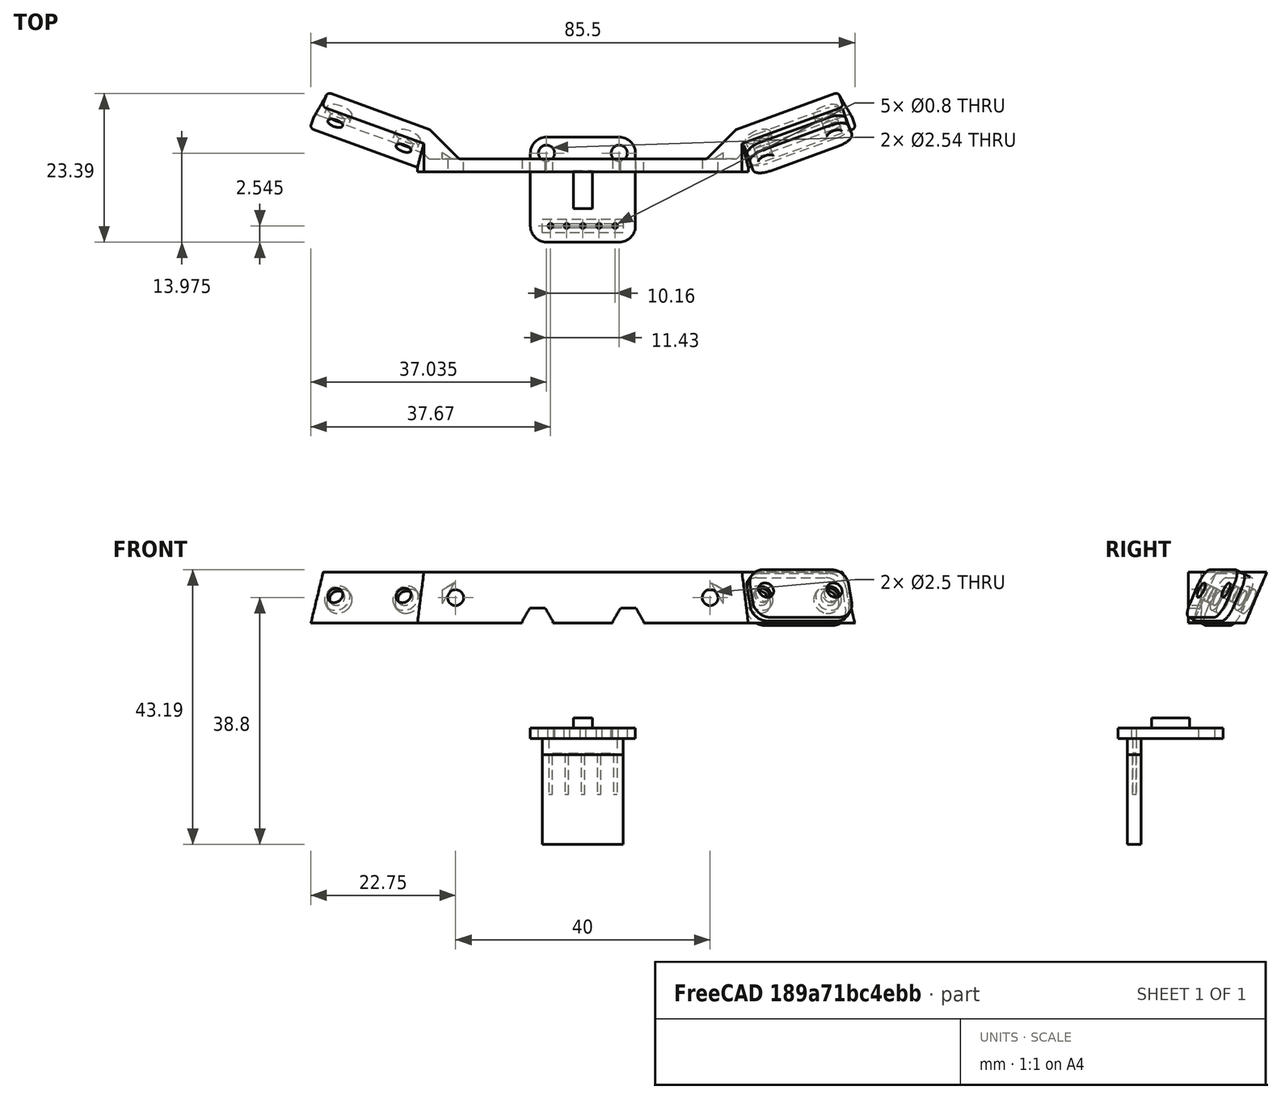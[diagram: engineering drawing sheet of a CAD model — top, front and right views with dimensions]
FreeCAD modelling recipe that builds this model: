
FCSTD DOCUMENT  (FreeCAD 0.19R24276 (Git))
Label: PB3D_Triplate_USMtToLightSens
License: All rights reserved
LicenseURL: http://en.wikipedia.org/wiki/All_rights_reserved
objects: Sketcher::SketchObject×29, PartDesign::Pocket×15, PartDesign::Body×13, PartDesign::Pad×12, PartDesign::Plane×11, PartDesign::LinearPattern×4, App::Part×3, Spreadsheet::Sheet×2, PartDesign::CoordinateSystem×2, Mesh::Feature×2, PartDesign::AdditiveLoft×1
note: 115 computed .brp shape members not serialized (recipe doc carries the construction recipe); baked Part::Feature solids carry a one-line shape summary decoded from their .brp

FEATURE [Spreadsheet::Sheet] Spreadsheet  label="params"
  cells = A1=M2 Bolt Clearances; C1=M2.5 Bolt Clearances; A2=Hole Clear Diam; B2(m2_hole_clear_diam)==2.5mm; C2=Hole Clear Diam; D2(m25_hole_clear_diam)==2.8mm; E2=Std Rad; F2(std_rad)==2mm; A3=Head Clear Diam; B3(m2_head_clear_diam)==4.2mm; C3=Head Clear Diam; D3(m25_head_clear_diam)==5.2mm; E3=Std Rad Min; F3(std_rad_min)==0.6mm; A4=Head Min Depth; B4(m2_head_min_depth)==2mm; C4=Head Min Depth; D4(m25_head_min_depth)==2.3mm; E4=Std Tol Clear; F4(std_tol_clear)==0.3mm; A5=Nut Clear Flat; B5(m2_nut_clear_flat)==4.2mm; C5=Nut Clear Flat; D5(m25_nut_clear_flat)==5.2mm; A6=Nut Min Depth; B6(m2_nut_min_depth)==2mm; C6=Nut Min Depth; D6(m25_nut_min_depth)==2mm; A8=USR Mount; C8=Light Sens Cent Loc; E8=LightMt; A9=USR Mt Width; B9(usr_mt_width)==52mm; C9=LightSens Loc X; D9(lightsens_loc_x)==35mm; E9=LightMt Side Thick; F9(lightmt_thick_side)==2.4mm; A10=USR Mt Height; B10(usr_mt_height)==41.5mm; C10=LightSens Loc Y; D10(lightsens_loc_y)==4.5mm; E10=LightMt Cent Thick; F10(lightmt_thick_cent)==2mm; A11=USR Mt Vert Thick; B11(usr_mt_vert_thick_top)==4.8mm; C11=LightSens Loc Z; D11(lightsens_loc_z)==16.5mm; E11=LightMt Leng Base; F11(lightmt_leng_base)==18mm; A12=USR Mt Vert Thick Bot; B12(usr_mt_vert_thick_bot)==8.4mm; C12=LightSens Ang X; D12(lightsens_ang_x)==65deg; E12=LightMt Leng Top; F12(lightmt_leng_top)==17mm; A13=USR Mt Foot Width; B13(usr_mt_foot_width)==32mm; C13=LightSens Ang Y; D13(lightsens_ang_y)==0deg; E13=LightMt Height; F13(lightmt_height)==8mm; C14=LightSens Ang Z; D14(lightsens_ang_z)==20deg; E14=LightMt Base Offset; F14(lightmt_base_offset)==3.5mm; A15=USR Mt Hole Cent Loc Z; B15(usr_mt_hole_cent_loc_z)==27mm; E15=LightMt Top Offset; F15(lightmt_top_offset)==lightmt_base_offset + lightmt_height / tan(lightsens_vert_slope_ang); A16=USR Mt Hole Width Long; B16(usr_mt_hole_width_long)==22.625mm; C16=LightSens Vert Slope Ang; D16(lightsens_vert_slope_ang)==lightsens_ang_x; E16=LightMt Z Dist to Mid Plate; F16(lightmt_z_dist_to_mid_plate)==3mm; A17=USR Mt Hole Width Short; B17(usr_mt_hole_width_short)==7.125mm; E17=LightMt Hole Space Leng; F17(lightmt_hole_space_leng)==40mm; A18=USR Mt Hole Height; B18(usr_mt_hole_height)==20.5mm; C18=LightSens Leng; D18(lightsens_leng)==16.51mm; C19=LightSens Width; D19(lightsens_width)==16.51mm; C20=LightSens Hole Width; D20(lightsens_hole_leng_space)==11.43mm; C21=LightSens Hole Edge Offset; D21(lightsens_hole_edge_offset)==2.54mm; C22=LightSens Hole Diam; D22(lightsens_hole_diam)==2.54mm
FEATURE [Spreadsheet::Sheet] Spreadsheet002  label="I2CLightParams"
  cells = A1=Inch to mm; B1(intomm)==25.4mm; E1=std tol; F1(std_tol)==0.3mm; A3=Adafruit I2C Exp; E3=Adafruit Temp I2C; I3=Adafruit Light; B4=Inch; C4=mm; F4=Inch; G4=mm; J4=Inch; K4=mm; A5=Length; B5=1.2; C5(exp_i2c_leng)==B5 * B$1; E5=Length; F5=0.8; G5(temp_leng)==F5 * $B$1; I5=Length; J5=0.65; K5(light_leng)==J5 * $B$1; A6=Width; B6=0.7; C6(exp_i2c_width)==B6 * B$1; E6=Width; F6=0.5; G6(temp_width)==F6 * $B$1; I6=Width; J6=0.65; K6(light_width)==J6 * $B$1; A7=Hole Leng Space; B7=1; C7(exp_i2c_hole_leng_space)==B7 * B$1; E7=Hole Leng Space; F7=0.6; G7(temp_hole_leng_space)==F7 * $B$1; I7=Hole Leng Space; J7=0.45; K7(light_hole_leng_space)==J7 * $B$1; A8=Hole Diam; B8=0.1; C8(exp_i2c_hole_mt_diam)==B8 * B$1; E8=Hole Diam; F8=0.1; G8(temp_hole_diam)==F8 * $B$1; I8=Hole Diam; J8=0.1; K8(light_hole_diam)==J8 * $B$1; A9=Num Pins; B9(exp_i2c_num_pins)=12; E9=Hole Edge Offset; F9=0.1; G9(temp_hole_edge_offset)==F9 * $B$1; I9=Hole Edge Offset; J9=0.1; K9(light_hole_edge_offset)==J9 * $B$1; A10=Pin Width Space; B10=0.6; C10(exp_i2c_pin_width_space)==B10 * B$1; E10=Pin Edge Offset; F10=0.09; G10(temp_pin_edge_offset)==F10 * $B$1; I10=Pin Edge Offset; J10=0.1; K10(light_pin_edge_offset)==J10 * $B$1; E11=Num Pins; F11(temp_num_pins)=8; I11=Num Pins; J11(light_num_pins)=5; A12=General Parameters; A13=Board Thick; B13(board_thickness)==1.65mm; A15=Pin Hole Diam; B15(pin_hole_diam)==0.8mm; A16=Pin Hole Space; B16(pin_hole_space)==2.54mm; A17=Pin Width; B17(pin_width)==0.6mm; A18=Pin Square Block Dim; B18(pin_square_block_dim)==2.54mm; A19=Pin Leng; B19(pin_leng)==6.2mm; A20=Pin Jumper Leng; B20(pin_jumper_leng)==14.1mm; A21=Pin Spacing; B21(pin_spacing)==2.54mm
FEATURE [Sketcher::SketchObject] Sketch049
  FullyConstrained = true
  MapMode = 5
  Support = -> [XY_Plane038]
  expr: Constraints[16] = <<I2CLightParams>>.light_leng
  expr: Constraints[17] = <<I2CLightParams>>.light_width
  expr: Constraints[18] = <<I2CLightParams>>.light_hole_diam
  sketch-geometry (8):
    g0: LineSegment StartX=-5.715 StartY=8.255 StartZ=0 EndX=5.715 EndY=8.255 EndZ=0
    g1: LineSegment StartX=8.255 StartY=5.715 StartZ=0 EndX=8.255 EndY=-5.715 EndZ=0
    g2: LineSegment StartX=5.715 StartY=-8.255 StartZ=0 EndX=-5.715 EndY=-8.255 EndZ=0
    g3: LineSegment StartX=-8.255 StartY=-5.715 StartZ=0 EndX=-8.255 EndY=5.715 EndZ=0
    g4: ArcOfCircle CenterX=-5.715 CenterY=5.715 CenterZ=0 NormalX=0 NormalY=0 NormalZ=1 AngleXU=0 Radius=2.54 StartAngle=1.5708 EndAngle=3.14159
    g5: ArcOfCircle CenterX=5.715 CenterY=5.715 CenterZ=0 NormalX=0 NormalY=0 NormalZ=1 AngleXU=0 Radius=2.54 StartAngle=1.76e-14 EndAngle=1.5708
    g6: ArcOfCircle CenterX=5.715 CenterY=-5.715 CenterZ=0 NormalX=0 NormalY=0 NormalZ=1 AngleXU=0 Radius=2.54 StartAngle=4.71239 EndAngle=6.28319
    g7: ArcOfCircle CenterX=-5.715 CenterY=-5.715 CenterZ=0 NormalX=0 NormalY=0 NormalZ=1 AngleXU=0 Radius=2.54 StartAngle=3.14159 EndAngle=4.71239
  constraints (19):
    c: Horizontal(g0)
    c: Horizontal(g2)
    c: Vertical(g1)
    c: Vertical(g3)
    c: Tangent(g3,g4) = 1.5708
    c: Tangent(g0,g4) = 1.5708
    c: Tangent(g0,g5) = 1.5708
    c: Tangent(g1,g5) = 1.5708
    c: Tangent(g1,g6) = 1.5708
    c: Tangent(g2,g6) = 1.5708
    c: Tangent(g2,g7) = 1.5708
    c: Tangent(g3,g7) = 1.5708
    c: Equal(g4,g5)
    c: Equal(g5,g6)
    c: Equal(g6,g7)
    c: Symmetric(g7,g5,g-1)
    c: DistanceX(g3,g1) = 16.51
    c: DistanceY(g2,g0) = 16.51
    c: Radius(g5) = 2.54
FEATURE [Sketcher::SketchObject] Sketch048
  FullyConstrained = true
  MapMode = 5
  Support = -> [XY_Plane037]
  sketch-geometry (4):
    g0: LineSegment StartX=-1.5 StartY=3 StartZ=0 EndX=1.5 EndY=3 EndZ=0
    g1: LineSegment StartX=1.5 StartY=3 StartZ=0 EndX=1.5 EndY=-3 EndZ=0
    g2: LineSegment StartX=1.5 StartY=-3 StartZ=0 EndX=-1.5 EndY=-3 EndZ=0
    g3: LineSegment StartX=-1.5 StartY=-3 StartZ=0 EndX=-1.5 EndY=3 EndZ=0
  constraints (11):
    c: Coincident(g0,g1)
    c: Coincident(g1,g2)
    c: Coincident(g2,g3)
    c: Coincident(g3,g0)
    c: Horizontal(g0)
    c: Horizontal(g2)
    c: Vertical(g1)
    c: Vertical(g3)
    c: Symmetric(g2,g0,g-1)
    c: DistanceX(g0,g0) = 3
    c: DistanceY(g1,g1) = 6
FEATURE [Sketcher::SketchObject] Sketch052
  FullyConstrained = true
  MapMode = 5
  Placement = pos=(0,0,0) rot=(1,0,0;1.5708rad)
  Support = -> [XZ_Plane034]
  expr: Constraints[57] = <<I2CLightParams>>.pin_leng * 2
  expr: Constraints[58] = <<I2CLightParams>>.pin_square_block_dim - <<I2CLightParams>>.std_tol
  expr: Constraints[59] = <<I2CLightParams>>.pin_width
  expr: Constraints[61] = <<I2CLightParams>>.pin_spacing
  sketch-geometry (24):
    g0: LineSegment StartX=-2.24 StartY=14.64 StartZ=0 EndX=-0.3 EndY=14.64 EndZ=0
    g1: LineSegment StartX=-0.3 StartY=14.64 StartZ=0 EndX=-0.3 EndY=2.24 EndZ=0
    g2: LineSegment StartX=-0.3 StartY=2.24 StartZ=0 EndX=-2.24 EndY=2.24 EndZ=0
    g3: LineSegment StartX=-2.24 StartY=2.24 StartZ=0 EndX=-2.24 EndY=14.64 EndZ=0
    g4: LineSegment StartX=0.3 StartY=14.64 StartZ=0 EndX=2.24 EndY=14.64 EndZ=0
    g5: LineSegment StartX=2.24 StartY=14.64 StartZ=0 EndX=2.24 EndY=2.24 EndZ=0
    g6: LineSegment StartX=2.24 StartY=2.24 StartZ=0 EndX=0.3 EndY=2.24 EndZ=0
    g7: LineSegment StartX=0.3 StartY=2.24 StartZ=0 EndX=0.3 EndY=14.64 EndZ=0
    g8: LineSegment StartX=2.84 StartY=14.64 StartZ=0 EndX=4.78 EndY=14.64 EndZ=0
    g9: LineSegment StartX=4.78 StartY=14.64 StartZ=0 EndX=4.78 EndY=2.24 EndZ=0
    g10: LineSegment StartX=4.78 StartY=2.24 StartZ=0 EndX=2.84 EndY=2.24 EndZ=0
    g11: LineSegment StartX=2.84 StartY=2.24 StartZ=0 EndX=2.84 EndY=14.64 EndZ=0
    g12: LineSegment StartX=-4.78 StartY=14.64 StartZ=0 EndX=-2.84 EndY=14.64 EndZ=0
    g13: LineSegment StartX=-2.84 StartY=14.64 StartZ=0 EndX=-2.84 EndY=2.24 EndZ=0
    g14: LineSegment StartX=-2.84 StartY=2.24 StartZ=0 EndX=-4.78 EndY=2.24 EndZ=0
    g15: LineSegment StartX=-4.78 StartY=2.24 StartZ=0 EndX=-4.78 EndY=14.64 EndZ=0
    g16: LineSegment StartX=-2.84 StartY=14.64 StartZ=0 EndX=-2.24 EndY=14.64 EndZ=0
    g17: LineSegment StartX=-0.3 StartY=14.64 StartZ=0 EndX=0.3 EndY=14.64 EndZ=0
    g18: LineSegment StartX=2.24 StartY=14.64 StartZ=0 EndX=2.84 EndY=14.64 EndZ=0
    g19: LineSegment StartX=-2.84 StartY=2.24 StartZ=0 EndX=-2.24 EndY=2.24 EndZ=0
    g20: LineSegment StartX=-0.3 StartY=2.24 StartZ=0 EndX=0.3 EndY=2.24 EndZ=0
    g21: LineSegment StartX=2.24 StartY=2.24 StartZ=0 EndX=2.84 EndY=2.24 EndZ=0
    g22: GeomPoint X=0 Y=2.24 Z=0
    g23: GeomPoint X=2.54 Y=2.24 Z=0
  constraints (62):
    c: Coincident(g0,g1)
    c: Coincident(g1,g2)
    c: Coincident(g2,g3)
    c: Coincident(g3,g0)
    c: Horizontal(g0)
    c: Horizontal(g2)
    c: Vertical(g1)
    c: Vertical(g3)
    c: Coincident(g4,g5)
    c: Coincident(g5,g6)
    c: Coincident(g6,g7)
    c: Coincident(g7,g4)
    c: Horizontal(g4)
    c: Horizontal(g6)
    c: Vertical(g5)
    c: Vertical(g7)
    c: Coincident(g8,g9)
    c: Coincident(g9,g10)
    c: Coincident(g10,g11)
    c: Coincident(g11,g8)
    c: Horizontal(g8)
    c: Horizontal(g10)
    c: Vertical(g9)
    c: Vertical(g11)
    c: Coincident(g12,g13)
    c: Coincident(g13,g14)
    c: Coincident(g14,g15)
    c: Coincident(g15,g12)
    c: Horizontal(g12)
    c: Horizontal(g14)
    c: Vertical(g13)
    c: Vertical(g15)
    c: Equal(g12,g0)
    c: Equal(g0,g4)
    c: Equal(g4,g8)
    c: Coincident(g16,g12)
    c: Coincident(g16,g0)
    c: Coincident(g17,g0)
    c: Coincident(g17,g4)
    c: Horizontal(g17)
    c: Coincident(g18,g4)
    c: Coincident(g18,g8)
    c: Horizontal(g18)
    c: Coincident(g19,g13)
    c: Coincident(g19,g2)
    c: Coincident(g20,g1)
    c: Coincident(g20,g6)
    c: Coincident(g21,g5)
    c: Coincident(g21,g10)
    c: Equal(g16,g17)
    c: Equal(g17,g18)
    c: Horizontal(g16)
    c: Horizontal(g19)
    c: Horizontal(g20)
    c: Horizontal(g21)
    c: PointOnObject(g22,g-2)
    c: Symmetric(g1,g6,g22)
    c: DistanceY(g9,g9) = 12.4
    c: DistanceY(g-1,g22) = 2.24
    c: DistanceX(g17,g17) = 0.6
    c: Symmetric(g5,g10,g23)
    c: DistanceX(g22,g23) = 2.54
FEATURE [Sketcher::SketchObject] Sketch050
  FullyConstrained = true
  MapMode = 5
  Support = -> [XY_Plane038]
  expr: Constraints[6] = <<I2CLightParams>>.light_hole_diam
  expr: Constraints[7] = <<I2CLightParams>>.light_hole_leng_space
  expr: Constraints[8] = <<I2CLightParams>>.light_width / 2 - <<I2CLightParams>>.light_hole_edge_offset
  sketch-geometry (4):
    g0: Circle CenterX=-5.715 CenterY=5.715 CenterZ=0 NormalX=0 NormalY=0 NormalZ=1 AngleXU=0 Radius=1.27
    g1: Circle CenterX=5.715 CenterY=5.715 CenterZ=0 NormalX=0 NormalY=0 NormalZ=1 AngleXU=0 Radius=1.27
    g2: LineSegment StartX=-5.715 StartY=5.715 StartZ=0 EndX=5.715 EndY=5.715 EndZ=0
    g3: GeomPoint X=0 Y=5.715 Z=0
  constraints (9):
    c: Coincident(g2,g0)
    c: Coincident(g2,g1)
    c: Horizontal(g2)
    c: PointOnObject(g3,g-2)
    c: Symmetric(g0,g1,g3)
    c: Equal(g0,g1)
    c: Diameter(g1) = 2.54
    c: DistanceX(g2,g2) = 11.43
    c: DistanceY(g-1,g3) = 5.715
FEATURE [Sketcher::SketchObject] Sketch051
  FullyConstrained = true
  MapMode = 5
  Support = -> [XY_Plane038]
  expr: Constraints[2] = <<I2CLightParams>>.pin_hole_diam
  expr: Constraints[1] = <<I2CLightParams>>.light_width / 2 - <<I2CLightParams>>.light_hole_edge_offset
  sketch-geometry (1):
    g0: Circle CenterX=0 CenterY=-5.715 CenterZ=0 NormalX=0 NormalY=0 NormalZ=1 AngleXU=0 Radius=0.4
  constraints (3):
    c: PointOnObject(g0,g-2)
    c: DistanceY(g0,g-1) = 5.715
    c: Diameter(g0) = 0.8
FEATURE [Sketcher::SketchObject] Sketch057
  FullyConstrained = true
  MapMode = 5
  Support = -> [XY_Plane044]
  expr: Constraints[1] = <<I2CLightParams>>.light_width / 2 - <<I2CLightParams>>.light_hole_edge_offset
  expr: Constraints[2] = <<I2CLightParams>>.pin_hole_diam
  sketch-geometry (1):
    g0: Circle CenterX=0 CenterY=-5.715 CenterZ=0 NormalX=0 NormalY=0 NormalZ=1 AngleXU=0 Radius=0.4
  constraints (3):
    c: PointOnObject(g0,g-2)
    c: DistanceY(g0,g-1) = 5.715
    c: Diameter(g0) = 0.8
FEATURE [Sketcher::SketchObject] Sketch055
  FullyConstrained = true
  MapMode = 5
  Support = -> [XY_Plane033]
  expr: Constraints[12] = <<I2CLightParams>>.pin_square_block_dim * (<<I2CLightParams>>.light_num_pins - 1) + <<I2CLightParams>>.pin_width
  expr: Constraints[11] = <<I2CLightParams>>.pin_width
  expr: Constraints[10] = <<I2CLightParams>>.light_width / 2 - <<I2CLightParams>>.light_hole_edge_offset
  sketch-geometry (5):
    g0: LineSegment StartX=-5.38 StartY=-5.415 StartZ=0 EndX=5.38 EndY=-5.415 EndZ=0
    g1: LineSegment StartX=5.38 StartY=-5.415 StartZ=0 EndX=5.38 EndY=-6.015 EndZ=0
    g2: LineSegment StartX=5.38 StartY=-6.015 StartZ=0 EndX=-5.38 EndY=-6.015 EndZ=0
    g3: LineSegment StartX=-5.38 StartY=-6.015 StartZ=0 EndX=-5.38 EndY=-5.415 EndZ=0
    g4: GeomPoint X=0 Y=-5.715 Z=0
  constraints (13):
    c: Coincident(g0,g1)
    c: Coincident(g1,g2)
    c: Coincident(g2,g3)
    c: Coincident(g3,g0)
    c: Horizontal(g0)
    c: Horizontal(g2)
    c: Vertical(g1)
    c: Vertical(g3)
    c: PointOnObject(g4,g-2)
    c: Symmetric(g2,g0,g4)
    c: DistanceY(g4,g-1) = 5.715
    c: DistanceY(g1,g1) = 0.6
    c: DistanceX(g2,g2) = 10.76
FEATURE [Sketcher::SketchObject] Sketch053
  FullyConstrained = false
  MapMode = 5
  Support = -> [XY_Plane035]
  expr: Constraints[11] = <<I2CLightParams>>.light_width / 2 - <<I2CLightParams>>.light_hole_edge_offset
  expr: Constraints[10] = <<I2CLightParams>>.pin_square_block_dim * <<I2CLightParams>>.light_num_pins
  sketch-geometry (5):
    g0: LineSegment StartX=-6.35 StartY=-4.6212 StartZ=0 EndX=6.35 EndY=-4.6212 EndZ=0
    g1: LineSegment StartX=6.35 StartY=-4.6212 StartZ=0 EndX=6.35 EndY=-6.8088 EndZ=0
    g2: LineSegment StartX=6.35 StartY=-6.8088 StartZ=0 EndX=-6.35 EndY=-6.8088 EndZ=0
    g3: LineSegment StartX=-6.35 StartY=-6.8088 StartZ=0 EndX=-6.35 EndY=-4.6212 EndZ=0
    g4: GeomPoint X=0 Y=-5.715 Z=0
  constraints (12):
    c: Coincident(g0,g1)
    c: Coincident(g1,g2)
    c: Coincident(g2,g3)
    c: Coincident(g3,g0)
    c: Horizontal(g0)
    c: Horizontal(g2)
    c: Vertical(g1)
    c: Vertical(g3)
    c: PointOnObject(g4,g-2)
    c: Symmetric(g2,g0,g4)
    c: DistanceX(g2,g2) = 12.7
    c: DistanceY(g4,g-1) = 5.715
FEATURE [Sketcher::SketchObject] Sketch054
  FullyConstrained = false
  MapMode = 5
  Support = -> [XY_Plane034]
  expr: Constraints[10] = <<I2CLightParams>>.pin_square_block_dim * <<I2CLightParams>>.light_num_pins
  expr: Constraints[11] = <<I2CLightParams>>.light_width / 2 - <<I2CLightParams>>.light_hole_edge_offset
  sketch-geometry (5):
    g0: LineSegment StartX=-6.35 StartY=-4.6212 StartZ=0 EndX=6.35 EndY=-4.6212 EndZ=0
    g1: LineSegment StartX=6.35 StartY=-4.6212 StartZ=0 EndX=6.35 EndY=-6.8088 EndZ=0
    g2: LineSegment StartX=6.35 StartY=-6.8088 StartZ=0 EndX=-6.35 EndY=-6.8088 EndZ=0
    g3: LineSegment StartX=-6.35 StartY=-6.8088 StartZ=0 EndX=-6.35 EndY=-4.6212 EndZ=0
    g4: GeomPoint X=0 Y=-5.715 Z=0
  constraints (12):
    c: Coincident(g0,g1)
    c: Coincident(g1,g2)
    c: Coincident(g2,g3)
    c: Coincident(g3,g0)
    c: Horizontal(g0)
    c: Horizontal(g2)
    c: Vertical(g1)
    c: Vertical(g3)
    c: PointOnObject(g4,g-2)
    c: Symmetric(g2,g0,g4)
    c: DistanceX(g2,g2) = 12.7
    c: DistanceY(g4,g-1) = 5.715
FEATURE [Sketcher::SketchObject] Sketch056
  FullyConstrained = true
  MapMode = 5
  Support = -> [XY_Plane039]
  sketch-geometry (4):
    g0: LineSegment StartX=-1.5 StartY=3 StartZ=0 EndX=1.5 EndY=3 EndZ=0
    g1: LineSegment StartX=1.5 StartY=3 StartZ=0 EndX=1.5 EndY=-3 EndZ=0
    g2: LineSegment StartX=1.5 StartY=-3 StartZ=0 EndX=-1.5 EndY=-3 EndZ=0
    g3: LineSegment StartX=-1.5 StartY=-3 StartZ=0 EndX=-1.5 EndY=3 EndZ=0
  constraints (11):
    c: Coincident(g0,g1)
    c: Coincident(g1,g2)
    c: Coincident(g2,g3)
    c: Coincident(g3,g0)
    c: Horizontal(g0)
    c: Horizontal(g2)
    c: Vertical(g1)
    c: Vertical(g3)
    c: Symmetric(g2,g0,g-1)
    c: DistanceX(g0,g0) = 3
    c: DistanceY(g1,g1) = 6
FEATURE [Sketcher::SketchObject] Sketch058
  FullyConstrained = true
  MapMode = 5
  Placement = pos=(0,0,0) rot=(1,0,0;1.5708rad)
  Support = -> [XZ_Plane042]
  expr: Constraints[61] = <<I2CLightParams>>.pin_spacing
  expr: Constraints[59] = <<I2CLightParams>>.pin_width
  expr: Constraints[58] = <<I2CLightParams>>.pin_square_block_dim - <<I2CLightParams>>.std_tol
  expr: Constraints[57] = <<I2CLightParams>>.pin_leng * 2
  sketch-geometry (24):
    g0: LineSegment StartX=-2.24 StartY=14.64 StartZ=0 EndX=-0.3 EndY=14.64 EndZ=0
    g1: LineSegment StartX=-0.3 StartY=14.64 StartZ=0 EndX=-0.3 EndY=2.24 EndZ=0
    g2: LineSegment StartX=-0.3 StartY=2.24 StartZ=0 EndX=-2.24 EndY=2.24 EndZ=0
    g3: LineSegment StartX=-2.24 StartY=2.24 StartZ=0 EndX=-2.24 EndY=14.64 EndZ=0
    g4: LineSegment StartX=0.3 StartY=14.64 StartZ=0 EndX=2.24 EndY=14.64 EndZ=0
    g5: LineSegment StartX=2.24 StartY=14.64 StartZ=0 EndX=2.24 EndY=2.24 EndZ=0
    g6: LineSegment StartX=2.24 StartY=2.24 StartZ=0 EndX=0.3 EndY=2.24 EndZ=0
    g7: LineSegment StartX=0.3 StartY=2.24 StartZ=0 EndX=0.3 EndY=14.64 EndZ=0
    g8: LineSegment StartX=2.84 StartY=14.64 StartZ=0 EndX=4.78 EndY=14.64 EndZ=0
    g9: LineSegment StartX=4.78 StartY=14.64 StartZ=0 EndX=4.78 EndY=2.24 EndZ=0
    g10: LineSegment StartX=4.78 StartY=2.24 StartZ=0 EndX=2.84 EndY=2.24 EndZ=0
    g11: LineSegment StartX=2.84 StartY=2.24 StartZ=0 EndX=2.84 EndY=14.64 EndZ=0
    g12: LineSegment StartX=-4.78 StartY=14.64 StartZ=0 EndX=-2.84 EndY=14.64 EndZ=0
    g13: LineSegment StartX=-2.84 StartY=14.64 StartZ=0 EndX=-2.84 EndY=2.24 EndZ=0
    g14: LineSegment StartX=-2.84 StartY=2.24 StartZ=0 EndX=-4.78 EndY=2.24 EndZ=0
    g15: LineSegment StartX=-4.78 StartY=2.24 StartZ=0 EndX=-4.78 EndY=14.64 EndZ=0
    g16: LineSegment StartX=-2.84 StartY=14.64 StartZ=0 EndX=-2.24 EndY=14.64 EndZ=0
    g17: LineSegment StartX=-0.3 StartY=14.64 StartZ=0 EndX=0.3 EndY=14.64 EndZ=0
    g18: LineSegment StartX=2.24 StartY=14.64 StartZ=0 EndX=2.84 EndY=14.64 EndZ=0
    g19: LineSegment StartX=-2.84 StartY=2.24 StartZ=0 EndX=-2.24 EndY=2.24 EndZ=0
    g20: LineSegment StartX=-0.3 StartY=2.24 StartZ=0 EndX=0.3 EndY=2.24 EndZ=0
    g21: LineSegment StartX=2.24 StartY=2.24 StartZ=0 EndX=2.84 EndY=2.24 EndZ=0
    g22: GeomPoint X=0 Y=2.24 Z=0
    g23: GeomPoint X=2.54 Y=2.24 Z=0
  constraints (62):
    c: Coincident(g0,g1)
    c: Coincident(g1,g2)
    c: Coincident(g2,g3)
    c: Coincident(g3,g0)
    c: Horizontal(g0)
    c: Horizontal(g2)
    c: Vertical(g1)
    c: Vertical(g3)
    c: Coincident(g4,g5)
    c: Coincident(g5,g6)
    c: Coincident(g6,g7)
    c: Coincident(g7,g4)
    c: Horizontal(g4)
    c: Horizontal(g6)
    c: Vertical(g5)
    c: Vertical(g7)
    c: Coincident(g8,g9)
    c: Coincident(g9,g10)
    c: Coincident(g10,g11)
    c: Coincident(g11,g8)
    c: Horizontal(g8)
    c: Horizontal(g10)
    c: Vertical(g9)
    c: Vertical(g11)
    c: Coincident(g12,g13)
    c: Coincident(g13,g14)
    c: Coincident(g14,g15)
    c: Coincident(g15,g12)
    c: Horizontal(g12)
    c: Horizontal(g14)
    c: Vertical(g13)
    c: Vertical(g15)
    c: Equal(g12,g0)
    c: Equal(g0,g4)
    c: Equal(g4,g8)
    c: Coincident(g16,g12)
    c: Coincident(g16,g0)
    c: Coincident(g17,g0)
    c: Coincident(g17,g4)
    c: Horizontal(g17)
    c: Coincident(g18,g4)
    c: Coincident(g18,g8)
    c: Horizontal(g18)
    c: Coincident(g19,g13)
    c: Coincident(g19,g2)
    c: Coincident(g20,g1)
    c: Coincident(g20,g6)
    c: Coincident(g21,g5)
    c: Coincident(g21,g10)
    c: Equal(g16,g17)
    c: Equal(g17,g18)
    c: Horizontal(g16)
    c: Horizontal(g19)
    c: Horizontal(g20)
    c: Horizontal(g21)
    c: PointOnObject(g22,g-2)
    c: Symmetric(g1,g6,g22)
    c: DistanceY(g9,g9) = 12.4
    c: DistanceY(g-1,g22) = 2.24
    c: DistanceX(g17,g17) = 0.6
    c: Symmetric(g5,g10,g23)
    c: DistanceX(g22,g23) = 2.54
FEATURE [Sketcher::SketchObject] Sketch061
  FullyConstrained = false
  MapMode = 5
  Support = -> [XY_Plane042]
  expr: Constraints[11] = <<I2CLightParams>>.light_width / 2 - <<I2CLightParams>>.light_hole_edge_offset
  expr: Constraints[10] = <<I2CLightParams>>.pin_square_block_dim * <<I2CLightParams>>.light_num_pins
  sketch-geometry (5):
    g0: LineSegment StartX=-6.35 StartY=-4.6212 StartZ=0 EndX=6.35 EndY=-4.6212 EndZ=0
    g1: LineSegment StartX=6.35 StartY=-4.6212 StartZ=0 EndX=6.35 EndY=-6.8088 EndZ=0
    g2: LineSegment StartX=6.35 StartY=-6.8088 StartZ=0 EndX=-6.35 EndY=-6.8088 EndZ=0
    g3: LineSegment StartX=-6.35 StartY=-6.8088 StartZ=0 EndX=-6.35 EndY=-4.6212 EndZ=0
    g4: GeomPoint X=0 Y=-5.715 Z=0
  constraints (12):
    c: Coincident(g0,g1)
    c: Coincident(g1,g2)
    c: Coincident(g2,g3)
    c: Coincident(g3,g0)
    c: Horizontal(g0)
    c: Horizontal(g2)
    c: Vertical(g1)
    c: Vertical(g3)
    c: PointOnObject(g4,g-2)
    c: Symmetric(g2,g0,g4)
    c: DistanceX(g2,g2) = 12.7
    c: DistanceY(g4,g-1) = 5.715
FEATURE [Sketcher::SketchObject] Sketch059
  FullyConstrained = true
  MapMode = 5
  Support = -> [XY_Plane044]
  expr: Constraints[8] = <<I2CLightParams>>.light_width / 2 - <<I2CLightParams>>.light_hole_edge_offset
  expr: Constraints[7] = <<I2CLightParams>>.light_hole_leng_space
  expr: Constraints[6] = <<I2CLightParams>>.light_hole_diam
  sketch-geometry (4):
    g0: Circle CenterX=-5.715 CenterY=5.715 CenterZ=0 NormalX=0 NormalY=0 NormalZ=1 AngleXU=0 Radius=1.27
    g1: Circle CenterX=5.715 CenterY=5.715 CenterZ=0 NormalX=0 NormalY=0 NormalZ=1 AngleXU=0 Radius=1.27
    g2: LineSegment StartX=-5.715 StartY=5.715 StartZ=0 EndX=5.715 EndY=5.715 EndZ=0
    g3: GeomPoint X=0 Y=5.715 Z=0
  constraints (9):
    c: Coincident(g2,g0)
    c: Coincident(g2,g1)
    c: Horizontal(g2)
    c: PointOnObject(g3,g-2)
    c: Symmetric(g0,g1,g3)
    c: Equal(g0,g1)
    c: Diameter(g1) = 2.54
    c: DistanceX(g2,g2) = 11.43
    c: DistanceY(g-1,g3) = 5.715
FEATURE [Sketcher::SketchObject] Sketch060
  FullyConstrained = true
  MapMode = 5
  Support = -> [XY_Plane044]
  expr: Constraints[18] = <<I2CLightParams>>.light_hole_diam
  expr: Constraints[17] = <<I2CLightParams>>.light_width
  expr: Constraints[16] = <<I2CLightParams>>.light_leng
  sketch-geometry (8):
    g0: LineSegment StartX=-5.715 StartY=8.255 StartZ=0 EndX=5.715 EndY=8.255 EndZ=0
    g1: LineSegment StartX=8.255 StartY=5.715 StartZ=0 EndX=8.255 EndY=-5.715 EndZ=0
    g2: LineSegment StartX=5.715 StartY=-8.255 StartZ=0 EndX=-5.715 EndY=-8.255 EndZ=0
    g3: LineSegment StartX=-8.255 StartY=-5.715 StartZ=0 EndX=-8.255 EndY=5.715 EndZ=0
    g4: ArcOfCircle CenterX=-5.715 CenterY=5.715 CenterZ=0 NormalX=0 NormalY=0 NormalZ=1 AngleXU=0 Radius=2.54 StartAngle=1.5708 EndAngle=3.14159
    g5: ArcOfCircle CenterX=5.715 CenterY=5.715 CenterZ=0 NormalX=0 NormalY=0 NormalZ=1 AngleXU=0 Radius=2.54 StartAngle=1.76e-14 EndAngle=1.5708
    g6: ArcOfCircle CenterX=5.715 CenterY=-5.715 CenterZ=0 NormalX=0 NormalY=0 NormalZ=1 AngleXU=0 Radius=2.54 StartAngle=4.71239 EndAngle=6.28319
    g7: ArcOfCircle CenterX=-5.715 CenterY=-5.715 CenterZ=0 NormalX=0 NormalY=0 NormalZ=1 AngleXU=0 Radius=2.54 StartAngle=3.14159 EndAngle=4.71239
  constraints (19):
    c: Horizontal(g0)
    c: Horizontal(g2)
    c: Vertical(g1)
    c: Vertical(g3)
    c: Tangent(g3,g4) = 1.5708
    c: Tangent(g0,g4) = 1.5708
    c: Tangent(g0,g5) = 1.5708
    c: Tangent(g1,g5) = 1.5708
    c: Tangent(g1,g6) = 1.5708
    c: Tangent(g2,g6) = 1.5708
    c: Tangent(g2,g7) = 1.5708
    c: Tangent(g3,g7) = 1.5708
    c: Equal(g4,g5)
    c: Equal(g5,g6)
    c: Equal(g6,g7)
    c: Symmetric(g7,g5,g-1)
    c: DistanceX(g3,g1) = 16.51
    c: DistanceY(g2,g0) = 16.51
    c: Radius(g5) = 2.54
FEATURE [Sketcher::SketchObject] Sketch063
  FullyConstrained = false
  MapMode = 5
  Support = -> [XY_Plane041]
  expr: Constraints[10] = <<I2CLightParams>>.pin_square_block_dim * <<I2CLightParams>>.light_num_pins
  expr: Constraints[11] = <<I2CLightParams>>.light_width / 2 - <<I2CLightParams>>.light_hole_edge_offset
  sketch-geometry (5):
    g0: LineSegment StartX=-6.35 StartY=-4.6212 StartZ=0 EndX=6.35 EndY=-4.6212 EndZ=0
    g1: LineSegment StartX=6.35 StartY=-4.6212 StartZ=0 EndX=6.35 EndY=-6.8088 EndZ=0
    g2: LineSegment StartX=6.35 StartY=-6.8088 StartZ=0 EndX=-6.35 EndY=-6.8088 EndZ=0
    g3: LineSegment StartX=-6.35 StartY=-6.8088 StartZ=0 EndX=-6.35 EndY=-4.6212 EndZ=0
    g4: GeomPoint X=0 Y=-5.715 Z=0
  constraints (12):
    c: Coincident(g0,g1)
    c: Coincident(g1,g2)
    c: Coincident(g2,g3)
    c: Coincident(g3,g0)
    c: Horizontal(g0)
    c: Horizontal(g2)
    c: Vertical(g1)
    c: Vertical(g3)
    c: PointOnObject(g4,g-2)
    c: Symmetric(g2,g0,g4)
    c: DistanceX(g2,g2) = 12.7
    c: DistanceY(g4,g-1) = 5.715
FEATURE [Sketcher::SketchObject] Sketch062
  FullyConstrained = true
  MapMode = 5
  Support = -> [XY_Plane043]
  expr: Constraints[10] = <<I2CLightParams>>.light_width / 2 - <<I2CLightParams>>.light_hole_edge_offset
  expr: Constraints[11] = <<I2CLightParams>>.pin_width
  expr: Constraints[12] = <<I2CLightParams>>.pin_square_block_dim * (<<I2CLightParams>>.light_num_pins - 1) + <<I2CLightParams>>.pin_width
  sketch-geometry (5):
    g0: LineSegment StartX=-5.38 StartY=-5.415 StartZ=0 EndX=5.38 EndY=-5.415 EndZ=0
    g1: LineSegment StartX=5.38 StartY=-5.415 StartZ=0 EndX=5.38 EndY=-6.015 EndZ=0
    g2: LineSegment StartX=5.38 StartY=-6.015 StartZ=0 EndX=-5.38 EndY=-6.015 EndZ=0
    g3: LineSegment StartX=-5.38 StartY=-6.015 StartZ=0 EndX=-5.38 EndY=-5.415 EndZ=0
    g4: GeomPoint X=0 Y=-5.715 Z=0
  constraints (13):
    c: Coincident(g0,g1)
    c: Coincident(g1,g2)
    c: Coincident(g2,g3)
    c: Coincident(g3,g0)
    c: Horizontal(g0)
    c: Horizontal(g2)
    c: Vertical(g1)
    c: Vertical(g3)
    c: PointOnObject(g4,g-2)
    c: Symmetric(g2,g0,g4)
    c: DistanceY(g4,g-1) = 5.715
    c: DistanceY(g1,g1) = 0.6
    c: DistanceX(g2,g2) = 10.76
FEATURE [PartDesign::Pad] Pad027
  Direction = (1,1,1)
  Length = 1.6
  Length2 = 100
  Profile = -> Sketch056
  Type = 0
FEATURE [PartDesign::Body] Body034  label="LightSensor001"
  Group = -> [Sketch056,Pad027]
  Origin = -> Origin039
  Tip = -> Pad027
FEATURE [PartDesign::Pad] Pad020
  Direction = (1,1,1)
  Length = 1.6
  Length2 = 100
  Profile = -> Sketch048
  Type = 0
FEATURE [PartDesign::Body] Body031  label="LightSensor"
  Group = -> [Sketch048,Pad020]
  Origin = -> Origin034
  Tip = -> Pad020
FEATURE [PartDesign::Pad] Pad021
  Direction = (1,1,1)
  Length = 14.1
  Length2 = 100
  Profile = -> Sketch053
  Reversed = true
  Type = 0
  expr: Length = <<I2CLightParams>>.pin_jumper_leng
FEATURE [PartDesign::Body] Body032  label="JumperHeader002"
  Group = -> [Sketch053,Pad021]
  Origin = -> Origin038
  Placement = pos=(0,0,-4.2) rot=(0,0,1;0rad)
  Tip = -> Pad021
FEATURE [PartDesign::Pad] Pad022
  Direction = (1,1,1)
  Length = 2.54
  Length2 = 100
  Profile = -> Sketch054
  Type = 0
  expr: Length = <<I2CLightParams>>.pin_square_block_dim
FEATURE [PartDesign::Body] Body028  label="PinBlock002"
  Group = -> [Sketch054,Pad022]
  Origin = -> Origin037
  Placement = pos=(0,0,-4.2) rot=(0,0,1;0rad)
  Tip = -> Pad022
FEATURE [PartDesign::Pad] Pad024
  Direction = (1,1,1)
  Length = 8.74
  Length2 = 100
  Profile = -> Sketch062
  Type = 0
  expr: Length = <<I2CLightParams>>.pin_square_block_dim + <<I2CLightParams>>.pin_leng
FEATURE [PartDesign::Pocket] Pocket031
  BaseFeature = -> Pad024
  Length = 5
  Length2 = 100
  Midplane = true
  Profile = -> Sketch058
  Type = 1
FEATURE [PartDesign::Body] Body036  label="Pins003"
  Group = -> [Sketch062,Pad024,Sketch058,Pocket031]
  Origin = -> Origin041
  Placement = pos=(0,-11.4,-1.7) rot=(1,0,0;3.14159rad)
  Tip = -> Pocket031
FEATURE [PartDesign::Pad] Pad025
  Direction = (1,1,1)
  Length = 2.54
  Length2 = 100
  Profile = -> Sketch061
  Type = 0
  expr: Length = <<I2CLightParams>>.pin_square_block_dim
FEATURE [PartDesign::Body] Body035  label="PinBlock003"
  Group = -> [Sketch061,Pad025]
  Origin = -> Origin042
  Placement = pos=(0,0,-4.2) rot=(0,0,1;0rad)
  Tip = -> Pad025
FEATURE [PartDesign::Pad] Pad018
  Direction = (1,1,1)
  Length = 1.65
  Length2 = 100
  Profile = -> Sketch049
  Reversed = true
  Type = 0
  expr: Length = <<I2CLightParams>>.board_thickness
FEATURE [PartDesign::Pocket] Pocket030
  BaseFeature = -> Pad018
  Length = 5
  Length2 = 100
  Profile = -> Sketch050
  Type = 1
FEATURE [PartDesign::Pocket] Pocket029
  BaseFeature = -> Pocket030
  Length = 5
  Length2 = 100
  Profile = -> Sketch051
  Type = 1
FEATURE [PartDesign::Pad] Pad019
  Direction = (1,1,1)
  Length = 8.74
  Length2 = 100
  Profile = -> Sketch055
  Type = 0
  expr: Length = <<I2CLightParams>>.pin_square_block_dim + <<I2CLightParams>>.pin_leng
FEATURE [PartDesign::Pocket] Pocket028
  BaseFeature = -> Pad019
  Length = 5
  Length2 = 100
  Midplane = true
  Profile = -> Sketch052
  Type = 1
FEATURE [PartDesign::Body] Body029  label="Pins002"
  Group = -> [Sketch055,Pad019,Sketch052,Pocket028]
  Origin = -> Origin036
  Placement = pos=(0,-11.4,-1.7) rot=(1,0,0;3.14159rad)
  Tip = -> Pocket028
FEATURE [PartDesign::Pad] Pad023
  Direction = (1,1,1)
  Length = 1.65
  Length2 = 100
  Profile = -> Sketch060
  Reversed = true
  Type = 0
  expr: Length = <<I2CLightParams>>.board_thickness
FEATURE [PartDesign::Pocket] Pocket033
  BaseFeature = -> Pad023
  Length = 5
  Length2 = 100
  Profile = -> Sketch059
  Type = 1
FEATURE [PartDesign::Pocket] Pocket032
  BaseFeature = -> Pocket033
  Length = 5
  Length2 = 100
  Profile = -> Sketch057
  Type = 1
FEATURE [PartDesign::LinearPattern] LinearPattern006
  BaseFeature = -> Pocket032
  Direction = -> X_Axis041
  Length = 5.08
  Occurrences = 3
  Originals = -> [Pocket032]
  expr: Length = <<I2CLightParams>>.pin_hole_space * 2
FEATURE [PartDesign::LinearPattern] LinearPattern007
  BaseFeature = -> LinearPattern006
  Direction = -> X_Axis041
  Length = 5.08
  Occurrences = 3
  Originals = -> [Pocket032]
  Reversed = true
  expr: Length = <<I2CLightParams>>.pin_hole_space * 2
FEATURE [PartDesign::Body] Body037  label="MainBoard003"
  Group = -> [Sketch060,Pad023,Sketch059,Pocket033,Sketch057,Pocket032,LinearPattern006,LinearPattern007]
  Origin = -> Origin040
  Tip = -> LinearPattern007
FEATURE [PartDesign::Pad] Pad026
  Direction = (1,1,1)
  Length = 14.1
  Length2 = 100
  Profile = -> Sketch063
  Reversed = true
  Type = 0
  expr: Length = <<I2CLightParams>>.pin_jumper_leng
FEATURE [PartDesign::Body] Body033  label="JumperHeader003"
  Group = -> [Sketch063,Pad026]
  Origin = -> Origin044
  Placement = pos=(0,0,-4.2) rot=(0,0,1;0rad)
  Tip = -> Pad026
FEATURE [App::Part] Part006  label="AdaF_I2CLight_Part2"
  Group = -> [Body037,Body034,Body035,Body036,Body033]
  Origin = -> Origin043
  Placement = pos=(35.62,2.7967,17.3452) rot=(0.950144,0.167536,0.262979;1.1813rad)
FEATURE [PartDesign::LinearPattern] LinearPattern004
  BaseFeature = -> Pocket029
  Direction = -> X_Axis036
  Length = 5.08
  Occurrences = 3
  Originals = -> [Pocket029]
  expr: Length = <<I2CLightParams>>.pin_hole_space * 2
FEATURE [PartDesign::LinearPattern] LinearPattern005
  BaseFeature = -> LinearPattern004
  Direction = -> X_Axis036
  Length = 5.08
  Occurrences = 3
  Originals = -> [Pocket029]
  Reversed = true
  expr: Length = <<I2CLightParams>>.pin_hole_space * 2
FEATURE [PartDesign::Body] Body030  label="MainBoard002"
  Group = -> [Sketch049,Pad018,Sketch050,Pocket030,Sketch051,Pocket029,LinearPattern004,LinearPattern005]
  Origin = -> Origin035
  Tip = -> LinearPattern005
FEATURE [App::Part] Part005  label="AdaF_I2CLight_Part1"
  Group = -> [Body030,Body031,Body028,Body029,Body032]
  Origin = -> Origin033
  Placement = pos=(-35,4.5,16.5) rot=(0.950144,-0.167536,-0.262979;1.1813rad)
FEATURE [Sketcher::SketchObject] Sketch  label="Sketch_MtLoft_Base"
  FullyConstrained = true
  MapMode = 5
  Support = -> [XY_Plane001]
  expr: Constraints[59] = <<params>>.lightmt_leng_base
  expr: Constraints[6] = <<params>>.usr_mt_width
  expr: Constraints[54] = 0.6mm
  expr: Constraints[5] = <<params>>.usr_mt_vert_thick_top
  expr: Constraints[22] = <<params>>.lightsens_ang_z
  expr: Constraints[52] = <<params>>.lightmt_thick_side
  expr: Constraints[38] = <<params>>.lightmt_base_offset
  expr: Constraints[29] = <<params>>.lightsens_ang_z
  expr: Constraints[37] = <<params>>.lightmt_thick_cent
  sketch-geometry (34):
    g0: LineSegment StartX=-26 StartY=2.8 StartZ=0 EndX=26 EndY=2.8 EndZ=0
    g1: LineSegment StartX=-23.8959 StartY=4.8 StartZ=0 EndX=23.8959 EndY=4.8 EndZ=0
    g2: GeomPoint X=0 Y=2.8 Z=0
    g3: GeomPoint X=0 Y=4.8 Z=0
    g4: LineSegment StartX=-26 StartY=2.8 StartZ=0 EndX=-42.3507 EndY=2.8 EndZ=0
    g5: LineSegment StartX=-42.3507 StartY=2.8 StartZ=0 EndX=-42.3507 EndY=9.45115 EndZ=0
    g6: LineSegment StartX=26 StartY=2.8 StartZ=0 EndX=42.3507 EndY=2.8 EndZ=0
    g7: LineSegment StartX=42.3507 StartY=2.8 StartZ=0 EndX=42.3507 EndY=9.45115 EndZ=0
    g8: LineSegment StartX=-26 StartY=2.8 StartZ=0 EndX=-26 EndY=3.5 EndZ=0
    g9: LineSegment StartX=-26 StartY=3.5 StartZ=0 EndX=-42.3507 EndY=9.45115 EndZ=0
    g10: LineSegment StartX=-42.7093 StartY=10.2202 StartZ=0 EndX=-42.2988 EndY=11.3478 EndZ=0
    g11: LineSegment StartX=-26 StartY=3.5 StartZ=0 EndX=-42.3507 EndY=3.5 EndZ=0
    g12: LineSegment StartX=26 StartY=2.8 StartZ=0 EndX=26 EndY=3.5 EndZ=0
    g13: LineSegment StartX=26 StartY=3.5 StartZ=0 EndX=42.3507 EndY=9.45115 EndZ=0
    g14: LineSegment StartX=42.7093 StartY=10.2202 StartZ=0 EndX=42.2988 EndY=11.3478 EndZ=0
    g15: LineSegment StartX=26 StartY=3.5 StartZ=0 EndX=42.3507 EndY=3.5 EndZ=0
    g16: LineSegment StartX=-41.5298 StartY=11.7064 StartZ=0 EndX=-25.1792 EndY=5.75526 EndZ=0
    g17: LineSegment StartX=-24.3201 StartY=4.97574 StartZ=0 EndX=-24.9601 EndY=5.61571 EndZ=0
    g18: LineSegment StartX=41.5298 StartY=11.7064 StartZ=0 EndX=25.1792 EndY=5.75526 EndZ=0
    g19: LineSegment StartX=24.9601 StartY=5.61571 StartZ=0 EndX=24.3201 EndY=4.97574 EndZ=0
    g20: ArcOfCircle CenterX=41.735 CenterY=11.1426 CenterZ=0 NormalX=0 NormalY=0 NormalZ=1 AngleXU=0 Radius=0.6 StartAngle=0.349066 EndAngle=1.91986
    g21: ArcOfCircle CenterX=42.1454 CenterY=10.015 CenterZ=0 NormalX=0 NormalY=0 NormalZ=1 AngleXU=0 Radius=0.6 StartAngle=5.06145 EndAngle=6.63225
    g22: ArcOfCircle CenterX=-42.1454 CenterY=10.015 CenterZ=0 NormalX=0 NormalY=0 NormalZ=1 AngleXU=0 Radius=0.6 StartAngle=2.79253 EndAngle=4.36332
    g23: ArcOfCircle CenterX=-41.735 CenterY=11.1426 CenterZ=0 NormalX=0 NormalY=0 NormalZ=1 AngleXU=0 Radius=0.6 StartAngle=1.22173 EndAngle=2.79253
    g24: LineSegment StartX=-42.3507 StartY=9.45115 StartZ=0 EndX=-41.5298 EndY=11.7064 EndZ=0
    g25: LineSegment StartX=-26 StartY=3.5 StartZ=0 EndX=-25.1792 EndY=5.75526 EndZ=0
    g26: LineSegment StartX=-42.7093 StartY=10.2202 StartZ=0 EndX=-25.7948 EndY=4.06382 EndZ=0
    g27: ArcOfCircle CenterX=25.3844 CenterY=5.19145 CenterZ=0 NormalX=0 NormalY=0 NormalZ=1 AngleXU=0 Radius=0.6 StartAngle=1.91986 EndAngle=2.35619
    g28: ArcOfCircle CenterX=23.8959 CenterY=5.4 CenterZ=0 NormalX=0 NormalY=0 NormalZ=1 AngleXU=0 Radius=0.6 StartAngle=4.71239 EndAngle=5.49779
    g29: LineSegment StartX=26 StartY=3.5 StartZ=0 EndX=25.1792 EndY=5.75526 EndZ=0
    g30: LineSegment StartX=24.3201 StartY=4.97574 StartZ=0 EndX=25.4629 EndY=4.97574 EndZ=0
    g31: ArcOfCircle CenterX=-25.3844 CenterY=5.19145 CenterZ=0 NormalX=0 NormalY=0 NormalZ=1 AngleXU=0 Radius=0.6 StartAngle=0.785398 EndAngle=1.22173
    g32: ArcOfCircle CenterX=-23.8959 CenterY=5.4 CenterZ=0 NormalX=0 NormalY=0 NormalZ=1 AngleXU=0 Radius=0.6 StartAngle=3.92699 EndAngle=4.71239
    g33: LineSegment StartX=-24.3201 StartY=4.97574 StartZ=0 EndX=-25.4629 EndY=4.97574 EndZ=0
  constraints (86):
    c: Horizontal(g0)
    c: Horizontal(g1)
    c: PointOnObject(g2,g-2)
    c: PointOnObject(g3,g-2)
    c: Symmetric(g0,g0,g2)
    c: DistanceY(g-1,g3) = 4.8
    c: DistanceX(g0,g0) = 52
    c: Coincident(g4,g0)
    c: Coincident(g5,g4)
    c: Horizontal(g4)
    c: Vertical(g5)
    c: Coincident(g6,g0)
    c: Horizontal(g6)
    c: Coincident(g7,g6)
    c: Vertical(g7)
    c: Coincident(g8,g0)
    c: Vertical(g8)
    c: Coincident(g9,g8)
    c: Perpendicular(g9,g10)
    c: Coincident(g11,g8)
    c: PointOnObject(g11,g5)
    c: Horizontal(g11)
    c: Angle(g9,g11) = 0.349066
    c: Coincident(g12,g0)
    c: Coincident(g13,g12)
    c: Vertical(g12)
    c: Coincident(g15,g12)
    c: PointOnObject(g15,g7)
    c: Horizontal(g15)
    c: Angle(g15,g13) = 0.349066
    c: Equal(g13,g9)
    c: Parallel(g9,g16)
    c: Equal(g9,g16)
    c: Parallel(g13,g18)
    c: Equal(g13,g18)
    c: Perpendicular(g14,g13)
    c: Equal(g14,g10)
    c: DistanceY(g2,g3) = 2
    c: DistanceY(g-1,g8) = 3.5
    c: Equal(g12,g8)
    c: Tangent(g18,g20) = -1.5708
    c: Tangent(g14,g20) = -1.5708
    c: Tangent(g14,g21) = -1.5708
    c: Tangent(g13,g21) = -1.5708
    c: Equal(g20,g21)
    c: Radius(g20) = 0.6
    c: Tangent(g9,g22) = 1.5708
    c: Tangent(g10,g22) = 1.5708
    c: Tangent(g10,g23) = 1.5708
    c: Tangent(g16,g23) = 1.5708
    c: Coincident(g24,g9)
    c: Coincident(g24,g16)
    c: Distance(g24) = 2.4
    c: Equal(g23,g22)
    c: Radius(g23) = 0.6
    c: Coincident(g25,g8)
    c: Coincident(g26,g10)
    c: PointOnObject(g26,g25)
    c: Perpendicular(g26,g25)
    c: Distance(g26) = 18
    c: Coincident(g7,g13)
    c: Coincident(g5,g9)
    c: Tangent(g19,g27) = -1.5708
    c: Tangent(g18,g27) = -1.5708
    c: Tangent(g19,g28) = 1.5708
    c: Tangent(g1,g28) = -1.5708
    c: Coincident(g29,g12)
    c: Coincident(g29,g18)
    c: Equal(g21,g27)
    c: Equal(g27,g28)
    c: Coincident(g30,g19)
    c: PointOnObject(g30,g29)
    c: Horizontal(g30)
    c: Angle(g30,g19) = 0.785398
    c: PointOnObject(g3,g1)
    c: Tangent(g16,g31) = 1.5708
    c: Tangent(g17,g31) = -1.5708
    c: Tangent(g17,g32) = 1.5708
    c: Tangent(g1,g32) = -1.5708
    c: Equal(g23,g31)
    c: Equal(g31,g32)
    c: Coincident(g33,g17)
    c: PointOnObject(g33,g25)
    c: Horizontal(g33)
    c: Angle(g17,g33) = 0.785398
    c: Coincident(g25,g16)
FEATURE [PartDesign::Plane] DatumPlane  label="Datum_MtLoft_Top"
  AttachmentOffset = pos=(0,0,8) rot=(0,0,1;0rad)
  Length = 98.5605
  MapMode = 5
  Placement = pos=(0,0,8) rot=(0,0,1;0rad)
  ResizeMode = 0
  Support = -> [XY_Plane001]
  Width = 63.0755
FEATURE [Sketcher::SketchObject] Sketch064  label="Sketch_MtLoft_Top"
  FullyConstrained = true
  MapMode = 5
  Placement = pos=(0,0,8) rot=(0,0,1;0rad)
  Support = -> [DatumPlane]
  expr: Constraints[67] = <<params>>.lightmt_leng_top
  expr: Constraints[43] = <<params>>.lightmt_thick_cent
  expr: Constraints[22] = <<params>>.lightsens_ang_z
  expr: Constraints[5] = <<params>>.usr_mt_vert_thick_top
  expr: Constraints[60] = <<params>>.std_rad_min
  expr: Constraints[6] = <<params>>.usr_mt_width - 2mm
  expr: Constraints[66] = <<params>>.lightmt_thick_side
  expr: Constraints[30] = <<params>>.lightsens_ang_z
  expr: Constraints[44] = <<params>>.lightmt_top_offset
  sketch-geometry (33):
    g0: LineSegment StartX=-25 StartY=2.8 StartZ=0 EndX=25 EndY=2.8 EndZ=0
    g1: LineSegment StartX=-19.1654 StartY=4.8 StartZ=0 EndX=19.1654 EndY=4.8 EndZ=0
    g2: GeomPoint X=0 Y=2.8 Z=0
    g3: GeomPoint X=0 Y=4.8 Z=0
    g4: LineSegment StartX=-25 StartY=2.8 StartZ=0 EndX=-40.411 EndY=2.8 EndZ=0
    g5: LineSegment StartX=-40.411 StartY=2.8 StartZ=0 EndX=-40.411 EndY=12.8396 EndZ=0
    g6: LineSegment StartX=25 StartY=2.8 StartZ=0 EndX=40.411 EndY=2.8 EndZ=0
    g7: LineSegment StartX=40.411 StartY=2.8 StartZ=0 EndX=40.411 EndY=12.8396 EndZ=0
    g8: LineSegment StartX=-25 StartY=2.8 StartZ=0 EndX=-25 EndY=7.23046 EndZ=0
    g9: LineSegment StartX=-25 StartY=7.23046 StartZ=0 EndX=-40.411 EndY=12.8396 EndZ=0
    g10: LineSegment StartX=-40.7696 StartY=13.6086 StartZ=0 EndX=-40.3591 EndY=14.7363 EndZ=0
    g11: LineSegment StartX=-25 StartY=7.23046 StartZ=0 EndX=-40.411 EndY=7.23046 EndZ=0
    g12: LineSegment StartX=25 StartY=2.8 StartZ=0 EndX=25 EndY=7.23046 EndZ=0
    g13: LineSegment StartX=25 StartY=7.23046 StartZ=0 EndX=40.411 EndY=12.8396 EndZ=0
    g14: LineSegment StartX=40.7696 StartY=13.6086 StartZ=0 EndX=40.3591 EndY=14.7363 EndZ=0
    g15: LineSegment StartX=25 StartY=7.23046 StartZ=0 EndX=40.411 EndY=7.23046 EndZ=0
    g16: LineSegment StartX=-39.5901 StartY=15.0949 StartZ=0 EndX=-24.1792 EndY=9.48572 EndZ=0
    g17: LineSegment StartX=39.5901 StartY=15.0949 StartZ=0 EndX=24.1792 EndY=9.48572 EndZ=0
    g18: LineSegment StartX=-23.9601 StartY=9.34617 StartZ=0 EndX=-19.5897 EndY=4.97574 EndZ=0
    g19: LineSegment StartX=23.9601 StartY=9.34617 StartZ=0 EndX=19.5897 EndY=4.97574 EndZ=0
    g20: LineSegment StartX=-19.5897 StartY=4.97574 StartZ=0 EndX=-25 EndY=4.97574 EndZ=0
    g21: LineSegment StartX=19.5897 StartY=4.97574 StartZ=0 EndX=25 EndY=4.97574 EndZ=0
    g22: ArcOfCircle CenterX=-40.2057 CenterY=13.4034 CenterZ=0 NormalX=0 NormalY=0 NormalZ=1 AngleXU=0 Radius=0.6 StartAngle=2.79253 EndAngle=4.36332
    g23: ArcOfCircle CenterX=-39.7953 CenterY=14.531 CenterZ=0 NormalX=0 NormalY=0 NormalZ=1 AngleXU=0 Radius=0.6 StartAngle=1.22173 EndAngle=2.79253
    g24: LineSegment StartX=-40.411 StartY=12.8396 StartZ=0 EndX=-39.5901 EndY=15.0949 EndZ=0
    g25: ArcOfCircle CenterX=-24.3844 CenterY=8.92191 CenterZ=0 NormalX=0 NormalY=0 NormalZ=1 AngleXU=0 Radius=0.6 StartAngle=0.785398 EndAngle=1.22173
    g26: ArcOfCircle CenterX=-19.1654 CenterY=5.4 CenterZ=0 NormalX=0 NormalY=0 NormalZ=1 AngleXU=0 Radius=0.6 StartAngle=3.92699 EndAngle=4.71239
    g27: LineSegment StartX=-25 StartY=7.23046 StartZ=0 EndX=-24.1792 EndY=9.48572 EndZ=0
    g28: LineSegment StartX=-40.7696 StartY=13.6086 StartZ=0 EndX=-24.7948 EndY=7.79428 EndZ=0
    g29: ArcOfCircle CenterX=40.2057 CenterY=13.4034 CenterZ=0 NormalX=0 NormalY=0 NormalZ=1 AngleXU=0 Radius=0.6 StartAngle=5.06145 EndAngle=6.63225
    g30: ArcOfCircle CenterX=39.7953 CenterY=14.531 CenterZ=0 NormalX=0 NormalY=0 NormalZ=1 AngleXU=0 Radius=0.6 StartAngle=0.349066 EndAngle=1.91986
    g31: ArcOfCircle CenterX=19.1654 CenterY=5.4 CenterZ=0 NormalX=0 NormalY=0 NormalZ=1 AngleXU=0 Radius=0.6 StartAngle=4.71239 EndAngle=5.49779
    g32: ArcOfCircle CenterX=24.3844 CenterY=8.92191 CenterZ=0 NormalX=0 NormalY=0 NormalZ=1 AngleXU=0 Radius=0.6 StartAngle=1.91986 EndAngle=2.35619
  constraints (84):
    c: Horizontal(g0)
    c: Horizontal(g1)
    c: PointOnObject(g2,g-2)
    c: PointOnObject(g3,g-2)
    c: Symmetric(g0,g0,g2)
    c: DistanceY(g-1,g3) = 4.8
    c: DistanceX(g0,g0) = 50
    c: Coincident(g4,g0)
    c: Coincident(g5,g4)
    c: Horizontal(g4)
    c: Vertical(g5)
    c: Coincident(g6,g0)
    c: Horizontal(g6)
    c: Coincident(g7,g6)
    c: Vertical(g7)
    c: Coincident(g8,g0)
    c: Vertical(g8)
    c: Coincident(g9,g8)
    c: Perpendicular(g9,g10)
    c: Coincident(g11,g8)
    c: PointOnObject(g11,g5)
    c: Horizontal(g11)
    c: Angle(g9,g11) = 0.349066
    c: Coincident(g12,g0)
    c: Coincident(g13,g12)
    c: Equal(g12,g8)
    c: Vertical(g12)
    c: Coincident(g15,g12)
    c: PointOnObject(g15,g7)
    c: Horizontal(g15)
    c: Angle(g15,g13) = 0.349066
    c: Equal(g13,g9)
    c: Parallel(g9,g16)
    c: Perpendicular(g14,g13)
    c: Equal(g10,g14)
    c: Equal(g17,g13)
    c: Parallel(g17,g13)
    c: Equal(g16,g9)
    c: PointOnObject(g20,g8)
    c: Horizontal(g20)
    c: PointOnObject(g21,g12)
    c: Horizontal(g21)
    c: Angle(g18,g20) = 0.785398
    c: DistanceY(g2,g3) = 2
    c: DistanceY(g-1,g8) = 7.23046
    c: Tangent(g9,g22) = 1.5708
    c: Tangent(g10,g22) = 1.5708
    c: Tangent(g10,g23) = 1.5708
    c: Tangent(g16,g23) = 1.5708
    c: Coincident(g5,g9)
    c: Equal(g22,g23)
    c: Coincident(g24,g9)
    c: Coincident(g24,g16)
    c: Tangent(g16,g25) = 1.5708
    c: Tangent(g18,g25) = 1.5708
    c: Tangent(g18,g26) = -1.5708
    c: Tangent(g1,g26) = -1.5708
    c: Coincident(g20,g18)
    c: Equal(g23,g25)
    c: Equal(g25,g26)
    c: Radius(g23) = 0.6
    c: Coincident(g27,g8)
    c: Coincident(g27,g16)
    c: Coincident(g28,g10)
    c: PointOnObject(g28,g27)
    c: Perpendicular(g28,g27)
    c: Distance(g24) = 2.4
    c: Distance(g28) = 17
    c: PointOnObject(g3,g1)
    c: Tangent(g13,g29) = -1.5708
    c: Tangent(g14,g29) = -1.5708
    c: Tangent(g14,g30) = -1.5708
    c: Tangent(g17,g30) = -1.5708
    c: Tangent(g1,g31) = -1.5708
    c: Tangent(g19,g31) = 1.5708
    c: Tangent(g19,g32) = -1.5708
    c: Tangent(g17,g32) = -1.5708
    c: Coincident(g21,g19)
    c: Angle(g21,g19) = 0.785398
    c: Equal(g31,g32)
    c: Equal(g32,g30)
    c: Equal(g30,g29)
    c: Equal(g31,g26)
    c: Coincident(g7,g13)
FEATURE [PartDesign::AdditiveLoft] AdditiveLoft  label="AddLoft_MainMtPlate"
  Closed = false
  Profile = -> Sketch
  Ruled = false
  Sections = -> [Sketch064]
FEATURE [PartDesign::Plane] DatumPlane001  label="Datum_LightSens_Left"
  AttachmentOffset = pos=(35,4.5,0) rot=(0.950144,0.167536,0.262979;1.1813rad)
  Length = 114.813
  MapMode = 5
  Placement = pos=(35,4.5,0) rot=(0.950144,0.167536,0.262979;1.1813rad)
  ResizeMode = 0
  Support = -> [XY_Plane001]
  Width = 94.9106
  expr: .AttachmentOffset.Rotation.Roll = <<params>>.lightsens_ang_x
  expr: .AttachmentOffset.Base.z = 0mm
  expr: .AttachmentOffset.Base.y = <<params>>.lightsens_loc_y
  expr: .AttachmentOffset.Rotation.Yaw = <<params>>.lightsens_ang_z
  expr: .AttachmentOffset.Base.x = <<params>>.lightsens_loc_x
FEATURE [PartDesign::Plane] DatumPlane002  label="Datum_LightSens_Right"
  AttachmentOffset = pos=(-35,4.5,0) rot=(0.950144,-0.167536,-0.262979;1.1813rad)
  Length = 114.813
  MapMode = 5
  Placement = pos=(-35,4.5,0) rot=(0.950144,-0.167536,-0.262979;1.1813rad)
  ResizeMode = 0
  Support = -> [XY_Plane001]
  Width = 94.9106
  expr: .AttachmentOffset.Rotation.Roll = <<params>>.lightsens_ang_x
  expr: .AttachmentOffset.Base.y = <<params>>.lightsens_loc_y
  expr: .AttachmentOffset.Rotation.Yaw = <<params>>.lightsens_ang_z * -1
  expr: .AttachmentOffset.Base.x = <<params>>.lightsens_loc_x * -1
FEATURE [Sketcher::SketchObject] Sketch065  label="Sketch_LightMtHoles_L"
  FullyConstrained = true
  MapMode = 5
  Placement = pos=(35,4.5,-4e-16) rot=(0.950144,0.167536,0.262979;1.1813rad)
  Support = -> [DatumPlane001]
  expr: Constraints[3] = <<params>>.lightsens_hole_leng_space
  expr: Constraints[4] = <<params>>.lightsens_width / 2 - <<params>>.lightsens_hole_edge_offset
  expr: Constraints[8] = <<params>>.m2_hole_clear_diam
  sketch-geometry (4):
    g0: LineSegment StartX=-5.715 StartY=5.715 StartZ=0 EndX=5.715 EndY=5.715 EndZ=0
    g1: GeomPoint X=0 Y=5.715 Z=0
    g2: Circle CenterX=5.715 CenterY=5.715 CenterZ=0 NormalX=0 NormalY=0 NormalZ=1 AngleXU=0 Radius=1.25
    g3: Circle CenterX=-5.715 CenterY=5.715 CenterZ=0 NormalX=0 NormalY=0 NormalZ=1 AngleXU=0 Radius=1.25
  constraints (9):
    c: Horizontal(g0)
    c: PointOnObject(g1,g-2)
    c: Symmetric(g0,g0,g1)
    c: DistanceX(g0,g0) = 11.43
    c: DistanceY(g-1,g1) = 5.715
    c: Coincident(g2,g0)
    c: Coincident(g3,g0)
    c: Equal(g3,g2)
    c: Diameter(g2) = 2.5
FEATURE [PartDesign::Pocket] Pocket  label="Pocket_LeftLightMtHoles"
  BaseFeature = -> AdditiveLoft
  Length = 5
  Length2 = 100
  Profile = -> Sketch065
  Type = 1
FEATURE [Sketcher::SketchObject] Sketch066  label="Sketch_LightMtHoles_L001"
  FullyConstrained = true
  MapMode = 5
  Placement = pos=(-35,4.5,-4e-16) rot=(0.950144,-0.167536,-0.262979;1.1813rad)
  Support = -> [DatumPlane002]
  expr: Constraints[8] = <<params>>.m2_hole_clear_diam
  expr: Constraints[4] = <<params>>.lightsens_width / 2 - <<params>>.lightsens_hole_edge_offset
  expr: Constraints[3] = <<params>>.lightsens_hole_leng_space
  sketch-geometry (4):
    g0: LineSegment StartX=-5.715 StartY=5.715 StartZ=0 EndX=5.715 EndY=5.715 EndZ=0
    g1: GeomPoint X=0 Y=5.715 Z=0
    g2: Circle CenterX=5.715 CenterY=5.715 CenterZ=0 NormalX=0 NormalY=0 NormalZ=1 AngleXU=0 Radius=1.25
    g3: Circle CenterX=-5.715 CenterY=5.715 CenterZ=0 NormalX=0 NormalY=0 NormalZ=1 AngleXU=0 Radius=1.25
  constraints (9):
    c: Horizontal(g0)
    c: PointOnObject(g1,g-2)
    c: Symmetric(g0,g0,g1)
    c: DistanceX(g0,g0) = 11.43
    c: DistanceY(g-1,g1) = 5.715
    c: Coincident(g2,g0)
    c: Coincident(g3,g0)
    c: Equal(g3,g2)
    c: Diameter(g2) = 2.5
FEATURE [PartDesign::Pocket] Pocket034  label="Pocket_RightLightMtHoles"
  BaseFeature = -> Pocket
  Length = 5
  Length2 = 100
  Profile = -> Sketch066
  Type = 1
FEATURE [Sketcher::SketchObject] Sketch067  label="Sketch_USRMtHoles"
  FullyConstrained = true
  MapMode = 5
  Placement = pos=(0,0,0) rot=(1,0,0;1.5708rad)
  Support = -> [XZ_Plane001]
  expr: Constraints[6] = <<params>>.lightmt_height / 2
  expr: Constraints[7] = <<params>>.lightmt_hole_space_leng
  expr: Constraints[8] = <<params>>.m2_hole_clear_diam
  sketch-geometry (4):
    g0: Circle CenterX=-20 CenterY=4 CenterZ=0 NormalX=0 NormalY=0 NormalZ=1 AngleXU=0 Radius=1.25
    g1: Circle CenterX=20 CenterY=4 CenterZ=0 NormalX=0 NormalY=0 NormalZ=1 AngleXU=0 Radius=1.25
    g2: LineSegment StartX=-20 StartY=4 StartZ=0 EndX=20 EndY=4 EndZ=0
    g3: GeomPoint X=0 Y=4 Z=0
  constraints (9):
    c: Coincident(g2,g0)
    c: Coincident(g2,g1)
    c: Horizontal(g2)
    c: PointOnObject(g3,g-2)
    c: Symmetric(g0,g1,g3)
    c: Equal(g0,g1)
    c: DistanceY(g-1,g3) = 4
    c: DistanceX(g2,g2) = 40
    c: Diameter(g1) = 2.5
FEATURE [PartDesign::Pocket] Pocket035  label="Pocket_ToUSRMtHoles"
  BaseFeature = -> Pocket034
  Length = 5
  Length2 = 100
  Profile = -> Sketch067
  Type = 1
FEATURE [PartDesign::Plane] DatumPlane003  label="Datum_BackOfCentPlate"
  AttachmentOffset = pos=(0,0,-4.8) rot=(0,0,1;0rad)
  Length = 98.5605
  MapMode = 5
  Placement = pos=(0,4.8,1.1e-15) rot=(1,0,0;1.5708rad)
  ResizeMode = 0
  Support = -> [XZ_Plane001]
  Width = 63.0755
  expr: .AttachmentOffset.Base.z = -1 * <<params>>.usr_mt_vert_thick_top
FEATURE [Sketcher::SketchObject] Sketch068  label="Sketch_USRHexSunk"
  FullyConstrained = true
  MapMode = 5
  Placement = pos=(0,4.8,1.1e-15) rot=(1,0,0;1.5708rad)
  Support = -> [DatumPlane003]
  expr: Constraints[48] = <<params>>.m2_nut_clear_flat
  expr: Constraints[8] = <<params>>.m2_hole_clear_diam
  expr: Constraints[7] = <<params>>.lightmt_hole_space_leng
  expr: Constraints[6] = <<params>>.lightmt_height / 2
  sketch-geometry (18):
    g0: Circle CenterX=-20 CenterY=4 CenterZ=0 NormalX=0 NormalY=0 NormalZ=1 AngleXU=0 Radius=1.25
    g1: Circle CenterX=20 CenterY=4 CenterZ=0 NormalX=0 NormalY=0 NormalZ=1 AngleXU=0 Radius=1.25
    g2: LineSegment StartX=-20 StartY=4 StartZ=0 EndX=20 EndY=4 EndZ=0
    g3: GeomPoint X=0 Y=4 Z=0
    g4: LineSegment StartX=-20 StartY=6.42487 StartZ=0 EndX=-22.1 EndY=5.21244 EndZ=0
    g5: LineSegment StartX=-22.1 StartY=5.21244 StartZ=0 EndX=-22.1 EndY=2.78756 EndZ=0
    g6: LineSegment StartX=-22.1 StartY=2.78756 StartZ=0 EndX=-20 EndY=1.57513 EndZ=0
    g7: LineSegment StartX=-20 StartY=1.57513 StartZ=0 EndX=-17.9 EndY=2.78756 EndZ=0
    g8: LineSegment StartX=-17.9 StartY=2.78756 StartZ=0 EndX=-17.9 EndY=5.21244 EndZ=0
    g9: LineSegment StartX=-17.9 StartY=5.21244 StartZ=0 EndX=-20 EndY=6.42487 EndZ=0
    g10: Circle CenterX=-20 CenterY=4 CenterZ=0 NormalX=0 NormalY=0 NormalZ=1 AngleXU=0 Radius=2.42487
    g11: LineSegment StartX=20 StartY=6.42487 StartZ=0 EndX=17.9 EndY=5.21244 EndZ=0
    g12: LineSegment StartX=17.9 StartY=5.21244 StartZ=0 EndX=17.9 EndY=2.78756 EndZ=0
    g13: LineSegment StartX=17.9 StartY=2.78756 StartZ=0 EndX=20 EndY=1.57513 EndZ=0
    g14: LineSegment StartX=20 StartY=1.57513 StartZ=0 EndX=22.1 EndY=2.78756 EndZ=0
    g15: LineSegment StartX=22.1 StartY=2.78756 StartZ=0 EndX=22.1 EndY=5.21244 EndZ=0
    g16: LineSegment StartX=22.1 StartY=5.21244 StartZ=0 EndX=20 EndY=6.42487 EndZ=0
    g17: Circle CenterX=20 CenterY=4 CenterZ=0 NormalX=0 NormalY=0 NormalZ=1 AngleXU=0 Radius=2.42487
  constraints (41):
    c: Coincident(g2,g0)
    c: Coincident(g2,g1)
    c: Horizontal(g2)
    c: PointOnObject(g3,g-2)
    c: Symmetric(g0,g1,g3)
    c: Equal(g0,g1)
    c: DistanceY(g-1,g3) = 4
    c: DistanceX(g2,g2) = 40
    c: Diameter(g1) = 2.5
    c: Coincident(g4,g5)
    c: Coincident(g5,g6)
    c: Coincident(g6,g7)
    c: Coincident(g7,g8)
    c: Coincident(g8,g9)
    c: Coincident(g9,g4)
    c: Equal(g4, g5-g9) x5
    c: PointOnObject(g4,g10)
    c: PointOnObject(g5,g10)
    c: PointOnObject(g6,g10)
    c: PointOnObject(g7,g10)
    c: PointOnObject(g8,g10)
    c: PointOnObject(g9,g10)
    c: Coincident(g10,g0)
    c: Coincident(g11,g12)
    c: Coincident(g12,g13)
    c: Coincident(g13,g14)
    c: Coincident(g14,g15)
    c: Coincident(g15,g16)
    c: Coincident(g16,g11)
    c: Equal(g11, g12-g16) x5
    c: PointOnObject(g11,g17)
    c: PointOnObject(g12,g17)
    c: PointOnObject(g13,g17)
    c: PointOnObject(g14,g17)
    c: PointOnObject(g15,g17)
    c: PointOnObject(g16,g17)
    c: Coincident(g17,g1)
    c: Vertical(g8)
    c: Vertical(g12)
    c: Equal(g17,g10)
    c: DistanceX(g5,g7) = 4.2
FEATURE [PartDesign::Pocket] Pocket036  label="Pocket_HexClearUSRMtHoles"
  BaseFeature = -> Pocket035
  Length = 5
  Length2 = 100
  Profile = -> Sketch068
  Type = 1
FEATURE [Sketcher::SketchObject] Sketch037  label="Sketch_USMtCSunk"
  FullyConstrained = true
  MapMode = 5
  Placement = pos=(0,0,0) rot=(1,0,0;1.5708rad)
  Support = -> [XZ_Plane001]
  expr: Constraints[176] = <<params>>.lightmt_height
  expr: Constraints[84] = <<params>>.usr_mt_hole_width_short
  expr: Constraints[72] = <<params>>.m2_nut_clear_flat
  expr: Constraints[69] = <<params>>.usr_mt_hole_width_long
  expr: Constraints[9] = <<params>>.usr_mt_hole_width_short
  expr: Constraints[11] = <<params>>.usr_mt_hole_cent_loc_z - <<params>>.lightsens_loc_z
  expr: Constraints[8] = <<params>>.usr_mt_hole_height
  sketch-geometry (63):
    g0: LineSegment StartX=-22.625 StartY=20.75 StartZ=0 EndX=7.125 EndY=20.75 EndZ=0
    g1: LineSegment StartX=7.125 StartY=20.75 StartZ=0 EndX=7.125 EndY=0.25 EndZ=0
    g2: LineSegment StartX=7.125 StartY=0.25 StartZ=0 EndX=-22.625 EndY=0.25 EndZ=0
    g3: LineSegment StartX=-22.625 StartY=0.25 StartZ=0 EndX=-22.625 EndY=20.75 EndZ=0
    g4: GeomPoint X=7.125 Y=10.5 Z=0
    g5: LineSegment StartX=-22.625 StartY=12.9249 StartZ=0 EndX=-24.725 EndY=11.7124 EndZ=0
    g6: LineSegment StartX=-24.725 StartY=11.7124 StartZ=0 EndX=-24.725 EndY=9.28756 EndZ=0
    g7: LineSegment StartX=-24.725 StartY=9.28756 StartZ=0 EndX=-22.625 EndY=8.07513 EndZ=0
    g8: LineSegment StartX=-22.625 StartY=8.07513 StartZ=0 EndX=-20.525 EndY=9.28756 EndZ=0
    g9: LineSegment StartX=-20.525 StartY=9.28756 StartZ=0 EndX=-20.525 EndY=11.7124 EndZ=0
    g10: LineSegment StartX=-20.525 StartY=11.7124 StartZ=0 EndX=-22.625 EndY=12.9249 EndZ=0
    g11: Circle CenterX=-22.625 CenterY=10.5 CenterZ=0 NormalX=0 NormalY=0 NormalZ=1 AngleXU=0 Radius=2.42487
    g12: LineSegment StartX=4.70013 StartY=20.75 StartZ=0 EndX=5.91256 EndY=18.65 EndZ=0
    g13: LineSegment StartX=5.91256 StartY=18.65 StartZ=0 EndX=8.33744 EndY=18.65 EndZ=0
    g14: LineSegment StartX=8.33744 StartY=18.65 StartZ=0 EndX=9.54987 EndY=20.75 EndZ=0
    g15: LineSegment StartX=9.54987 StartY=20.75 StartZ=0 EndX=8.33744 EndY=22.85 EndZ=0
    g16: LineSegment StartX=8.33744 StartY=22.85 StartZ=0 EndX=5.91256 EndY=22.85 EndZ=0
    g17: LineSegment StartX=5.91256 StartY=22.85 StartZ=0 EndX=4.70013 EndY=20.75 EndZ=0
    g18: Circle CenterX=7.125 CenterY=20.75 CenterZ=0 NormalX=0 NormalY=0 NormalZ=1 AngleXU=0 Radius=2.42487
    g19: LineSegment StartX=4.70013 StartY=0.25 StartZ=0 EndX=5.91256 EndY=-1.85 EndZ=0
    g20: LineSegment StartX=5.91256 StartY=-1.85 StartZ=0 EndX=8.33744 EndY=-1.85 EndZ=0
    g21: LineSegment StartX=8.33744 StartY=-1.85 StartZ=0 EndX=9.54987 EndY=0.25 EndZ=0
    g22: LineSegment StartX=9.54987 StartY=0.25 StartZ=0 EndX=8.33744 EndY=2.35 EndZ=0
    g23: LineSegment StartX=8.33744 StartY=2.35 StartZ=0 EndX=5.91256 EndY=2.35 EndZ=0
    g24: LineSegment StartX=5.91256 StartY=2.35 StartZ=0 EndX=4.70013 EndY=0.25 EndZ=0
    g25: Circle CenterX=7.125 CenterY=0.25 CenterZ=0 NormalX=0 NormalY=0 NormalZ=1 AngleXU=0 Radius=2.42487
    g26: LineSegment StartX=-7.125 StartY=20.75 StartZ=0 EndX=22.625 EndY=20.75 EndZ=0
    g27: LineSegment StartX=22.625 StartY=20.75 StartZ=0 EndX=22.625 EndY=0.25 EndZ=0
    g28: LineSegment StartX=22.625 StartY=0.25 StartZ=0 EndX=-7.125 EndY=0.25 EndZ=0
    g29: LineSegment StartX=-7.125 StartY=0.25 StartZ=0 EndX=-7.125 EndY=20.75 EndZ=0
    g30: LineSegment StartX=-4.70013 StartY=20.75 StartZ=0 EndX=-5.91256 EndY=22.85 EndZ=0
    g31: LineSegment StartX=-5.91256 StartY=22.85 StartZ=0 EndX=-8.33744 EndY=22.85 EndZ=0
    g32: LineSegment StartX=-8.33744 StartY=22.85 StartZ=0 EndX=-9.54987 EndY=20.75 EndZ=0
    g33: LineSegment StartX=-9.54987 StartY=20.75 StartZ=0 EndX=-8.33744 EndY=18.65 EndZ=0
    g34: LineSegment StartX=-8.33744 StartY=18.65 StartZ=0 EndX=-5.91256 EndY=18.65 EndZ=0
    g35: LineSegment StartX=-5.91256 StartY=18.65 StartZ=0 EndX=-4.70013 EndY=20.75 EndZ=0
    g36: Circle CenterX=-7.125 CenterY=20.75 CenterZ=0 NormalX=0 NormalY=0 NormalZ=1 AngleXU=0 Radius=2.42487
    g37: LineSegment StartX=-9.54987 StartY=0.25 StartZ=0 EndX=-8.33744 EndY=-1.85 EndZ=0
    g38: LineSegment StartX=-8.33744 StartY=-1.85 StartZ=0 EndX=-5.91256 EndY=-1.85 EndZ=0
    g39: LineSegment StartX=-5.91256 StartY=-1.85 StartZ=0 EndX=-4.70013 EndY=0.25 EndZ=0
    g40: LineSegment StartX=-4.70013 StartY=0.25 StartZ=0 EndX=-5.91256 EndY=2.35 EndZ=0
    g41: LineSegment StartX=-5.91256 StartY=2.35 StartZ=0 EndX=-8.33744 EndY=2.35 EndZ=0
    g42: LineSegment StartX=-8.33744 StartY=2.35 StartZ=0 EndX=-9.54987 EndY=0.25 EndZ=0
    g43: Circle CenterX=-7.125 CenterY=0.25 CenterZ=0 NormalX=0 NormalY=0 NormalZ=1 AngleXU=0 Radius=2.42487
    g44: LineSegment StartX=22.625 StartY=12.9249 StartZ=0 EndX=20.525 EndY=11.7124 EndZ=0
    g45: LineSegment StartX=20.525 StartY=11.7124 StartZ=0 EndX=20.525 EndY=9.28756 EndZ=0
    g46: LineSegment StartX=20.525 StartY=9.28756 StartZ=0 EndX=22.625 EndY=8.07513 EndZ=0
    g47: LineSegment StartX=22.625 StartY=8.07513 StartZ=0 EndX=24.725 EndY=9.28756 EndZ=0
    g48: LineSegment StartX=24.725 StartY=9.28756 StartZ=0 EndX=24.725 EndY=11.7124 EndZ=0
    g49: LineSegment StartX=24.725 StartY=11.7124 StartZ=0 EndX=22.625 EndY=12.9249 EndZ=0
    g50: Circle CenterX=22.625 CenterY=10.5 CenterZ=0 NormalX=0 NormalY=0 NormalZ=1 AngleXU=0 Radius=2.42487
    g51: LineSegment StartX=20.525 StartY=9.28756 StartZ=0 EndX=20.525 EndY=8.07513 EndZ=0
    g52: LineSegment StartX=24.725 StartY=9.28756 StartZ=0 EndX=24.725 EndY=8.07513 EndZ=0
    g53: LineSegment StartX=20.525 StartY=8.07513 StartZ=0 EndX=24.725 EndY=8.07513 EndZ=0
    g54: LineSegment StartX=-24.725 StartY=9.28756 StartZ=0 EndX=-24.725 EndY=8.07513 EndZ=0
    g55: LineSegment StartX=-20.525 StartY=9.28756 StartZ=0 EndX=-20.525 EndY=8.07513 EndZ=0
    g56: LineSegment StartX=-20.525 StartY=8.07513 StartZ=0 EndX=-24.725 EndY=8.07513 EndZ=0
    g57: LineSegment StartX=-9.54987 StartY=0.25 StartZ=0 EndX=-9.54987 EndY=-7.75 EndZ=0
    g58: LineSegment StartX=-4.70013 StartY=0.25 StartZ=0 EndX=-4.70013 EndY=-7.75 EndZ=0
    g59: LineSegment StartX=4.70013 StartY=0.25 StartZ=0 EndX=4.70013 EndY=-7.75 EndZ=0
    g60: LineSegment StartX=9.54987 StartY=0.25 StartZ=0 EndX=9.54987 EndY=-7.75 EndZ=0
    g61: LineSegment StartX=-9.54987 StartY=-7.75 StartZ=0 EndX=-4.70013 EndY=-7.75 EndZ=0
    g62: LineSegment StartX=4.70013 StartY=-7.75 StartZ=0 EndX=9.54987 EndY=-7.75 EndZ=0
  constraints (153):
    c: Coincident(g0,g1)
    c: Coincident(g1,g2)
    c: Coincident(g2,g3)
    c: Coincident(g3,g0)
    c: Horizontal(g0)
    c: Horizontal(g2)
    c: Vertical(g1)
    c: Vertical(g3)
    c: DistanceY(g1,g0) = 20.5
    c: DistanceX(g-1,g1) = 7.125
    c: Symmetric(g1,g0,g4)
    c: DistanceY(g-1,g4) = 10.5
    c: Coincident(g5,g6)
    c: Coincident(g6,g7)
    c: Coincident(g7,g8)
    c: Coincident(g8,g9)
    c: Coincident(g9,g10)
    c: Coincident(g10,g5)
    c: Equal(g5, g6-g10) x5
    c: PointOnObject(g5,g11)
    c: PointOnObject(g6,g11)
    c: PointOnObject(g7,g11)
    c: PointOnObject(g8,g11)
    c: PointOnObject(g9,g11)
    c: PointOnObject(g10,g11)
    c: Coincident(g12,g13)
    c: Coincident(g13,g14)
    c: Coincident(g14,g15)
    c: Coincident(g15,g16)
    c: Coincident(g16,g17)
    c: Coincident(g17,g12)
    c: Equal(g12, g13-g17) x5
    c: PointOnObject(g12,g18)
    c: PointOnObject(g13,g18)
    c: PointOnObject(g14,g18)
    c: PointOnObject(g15,g18)
    c: PointOnObject(g16,g18)
    c: PointOnObject(g17,g18)
    c: Coincident(g18,g0)
    c: PointOnObject(g17,g0)
    c: Coincident(g19,g20)
    c: Coincident(g20,g21)
    c: Coincident(g21,g22)
    c: Coincident(g22,g23)
    c: Coincident(g23,g24)
    c: Coincident(g24,g19)
    c: Equal(g19, g20-g24) x5
    c: PointOnObject(g19,g25)
    c: PointOnObject(g20,g25)
    c: PointOnObject(g21,g25)
    c: PointOnObject(g22,g25)
    c: PointOnObject(g23,g25)
    c: PointOnObject(g24,g25)
    c: Coincident(g25,g1)
    c: PointOnObject(g24,g2)
    c: Vertical(g6)
    c: Symmetric(g0,g2,g11)
    c: DistanceX(g2,g-1) = 22.625
    c: Equal(g25,g18)
    c: Equal(g18,g11)
    c: DistanceY(g13,g15) = 4.2
    c: Coincident(g26,g27)
    c: Coincident(g27,g28)
    c: Coincident(g28,g29)
    c: Coincident(g29,g26)
    c: Horizontal(g26)
    c: Horizontal(g28)
    c: Vertical(g27)
    c: Vertical(g29)
    c: PointOnObject(g26,g0)
    c: PointOnObject(g28,g2)
    c: Equal(g0,g26)
    c: DistanceX(g28,g-1) = 7.125
    c: Coincident(g30,g31)
    c: Coincident(g31,g32)
    c: Coincident(g32,g33)
    c: Coincident(g33,g34)
    c: Coincident(g34,g35)
    c: Coincident(g35,g30)
    c: Equal(g30, g31-g35) x5
    c: PointOnObject(g30,g36)
    c: PointOnObject(g31,g36)
    c: PointOnObject(g32,g36)
    c: PointOnObject(g33,g36)
    c: PointOnObject(g34,g36)
    c: PointOnObject(g35,g36)
    c: Coincident(g36,g26)
    c: PointOnObject(g35,g0)
    c: Coincident(g37,g38)
    c: Coincident(g38,g39)
    c: Coincident(g39,g40)
    c: Coincident(g40,g41)
    c: Coincident(g41,g42)
    c: Coincident(g42,g37)
    c: Equal(g37, g38-g42) x5
    c: PointOnObject(g37,g43)
    c: PointOnObject(g38,g43)
    c: PointOnObject(g39,g43)
    c: PointOnObject(g40,g43)
    c: PointOnObject(g41,g43)
    c: PointOnObject(g42,g43)
    c: Coincident(g43,g28)
    c: PointOnObject(g42,g2)
    c: Coincident(g44,g45)
    c: Coincident(g45,g46)
    c: Coincident(g46,g47)
    c: Coincident(g47,g48)
    c: Coincident(g48,g49)
    c: Coincident(g49,g44)
    c: Equal(g44, g45-g49) x5
    c: PointOnObject(g44,g50)
    c: PointOnObject(g45,g50)
    c: PointOnObject(g46,g50)
    c: PointOnObject(g47,g50)
    c: PointOnObject(g48,g50)
    c: PointOnObject(g49,g50)
    c: Vertical(g45)
    c: Symmetric(g26,g27,g50)
    c: Equal(g18,g36)
    c: Equal(g18,g50)
    c: Equal(g18,g43)
    c: Coincident(g51,g45)
    c: Vertical(g51)
    c: Coincident(g52,g48)
    c: Vertical(g52)
    c: Coincident(g53,g51)
    c: Coincident(g53,g52)
    c: Horizontal(g53)
    c: Coincident(g54,g6)
    c: Vertical(g54)
    c: Coincident(g55,g9)
    c: Vertical(g55)
    c: Coincident(g56,g55)
    c: Coincident(g56,g54)
    c: Horizontal(g56)
    c: Equal(g55,g52)
    c: PointOnObject(g46,g53)
    c: Coincident(g57,g42)
    c: Vertical(g57)
    c: Coincident(g58,g40)
    c: Vertical(g58)
    c: Coincident(g59,g24)
    c: Vertical(g59)
    c: Coincident(g60,g22)
    c: Vertical(g60)
    c: Coincident(g61,g57)
    c: Coincident(g61,g58)
    c: Horizontal(g61)
    c: Coincident(g62,g59)
    c: Coincident(g62,g60)
    c: Horizontal(g62)
    c: Equal(g58,g59)
    c: Distance(g58) = 8
FEATURE [PartDesign::Pocket] Pocket037  label="Pocket_ClearUSMtNuts"
  BaseFeature = -> Pocket036
  Length = 5
  Length2 = 100
  Profile = -> Sketch037
  Type = 1
FEATURE [PartDesign::CoordinateSystem] Local_CS  label="Local_CS_Left_LightSens"
  AttacherType = Attacher::AttachEngine3D
  MapMode = 5
  Placement = pos=(35,4.5,-4e-16) rot=(0.950144,0.167536,0.262979;1.1813rad)
  Support = -> [DatumPlane001]
FEATURE [PartDesign::CoordinateSystem] Local_CS001  label="Local_CS_Right_LightSens"
  AttacherType = Attacher::AttachEngine3D
  MapMode = 5
  Placement = pos=(-35,4.5,-4e-16) rot=(0.950144,-0.167536,-0.262979;1.1813rad)
  Support = -> [DatumPlane002]
FEATURE [PartDesign::Plane] DatumPlane004  label="Datum_Left_CSunk_LightSens"
  AttachmentOffset = pos=(0,0,-3) rot=(0,0,1;0rad)
  Length = 114.813
  MapMode = 5
  Placement = pos=(34.0701,7.05495,-1.26785) rot=(0.950144,0.167536,0.262979;1.1813rad)
  ResizeMode = 0
  Support = -> [Local_CS]
  Width = 94.9106
  expr: .AttachmentOffset.Base.z = <<params>>.lightmt_z_dist_to_mid_plate * -1
FEATURE [PartDesign::Plane] DatumPlane005  label="Datum_Right_CSunk_LightSens"
  AttachmentOffset = pos=(0,0,-3) rot=(0,0,1;0rad)
  Length = 114.813
  MapMode = 5
  Placement = pos=(-34.0701,7.05495,-1.26785) rot=(0.950144,-0.167536,-0.262979;1.1813rad)
  ResizeMode = 0
  Support = -> [Local_CS001]
  Width = 94.9106
  expr: .AttachmentOffset.Base.z = -1 * <<params>>.lightmt_z_dist_to_mid_plate
FEATURE [Sketcher::SketchObject] Sketch069  label="Sketch_LightMtHoles_L002"
  FullyConstrained = true
  MapMode = 5
  Placement = pos=(34.0701,7.05495,-1.26785) rot=(0.950144,0.167536,0.262979;1.1813rad)
  Support = -> [DatumPlane004]
  expr: Constraints[8] = <<params>>.m2_head_clear_diam
  expr: Constraints[4] = <<params>>.lightsens_width / 2 - <<params>>.lightsens_hole_edge_offset
  expr: Constraints[3] = <<params>>.lightsens_hole_leng_space
  sketch-geometry (4):
    g0: LineSegment StartX=-5.715 StartY=5.715 StartZ=0 EndX=5.715 EndY=5.715 EndZ=0
    g1: GeomPoint X=0 Y=5.715 Z=0
    g2: Circle CenterX=5.715 CenterY=5.715 CenterZ=0 NormalX=0 NormalY=0 NormalZ=1 AngleXU=0 Radius=2.1
    g3: Circle CenterX=-5.715 CenterY=5.715 CenterZ=0 NormalX=0 NormalY=0 NormalZ=1 AngleXU=0 Radius=2.1
  constraints (9):
    c: Horizontal(g0)
    c: PointOnObject(g1,g-2)
    c: Symmetric(g0,g0,g1)
    c: DistanceX(g0,g0) = 11.43
    c: DistanceY(g-1,g1) = 5.715
    c: Coincident(g2,g0)
    c: Coincident(g3,g0)
    c: Equal(g3,g2)
    c: Diameter(g2) = 4.2
FEATURE [Sketcher::SketchObject] Sketch070  label="Sketch_LightMtHoles_R"
  FullyConstrained = true
  MapMode = 5
  Placement = pos=(-34.0701,7.05495,-1.26785) rot=(0.950144,-0.167536,-0.262979;1.1813rad)
  Support = -> [DatumPlane005]
  expr: Constraints[8] = <<params>>.m2_head_clear_diam
  expr: Constraints[4] = <<params>>.lightsens_width / 2 - <<params>>.lightsens_hole_edge_offset
  expr: Constraints[3] = <<params>>.lightsens_hole_leng_space
  sketch-geometry (4):
    g0: LineSegment StartX=-5.715 StartY=5.715 StartZ=0 EndX=5.715 EndY=5.715 EndZ=0
    g1: GeomPoint X=0 Y=5.715 Z=0
    g2: Circle CenterX=5.715 CenterY=5.715 CenterZ=0 NormalX=0 NormalY=0 NormalZ=1 AngleXU=0 Radius=2.1
    g3: Circle CenterX=-5.715 CenterY=5.715 CenterZ=0 NormalX=0 NormalY=0 NormalZ=1 AngleXU=0 Radius=2.1
  constraints (9):
    c: Horizontal(g0)
    c: PointOnObject(g1,g-2)
    c: Symmetric(g0,g0,g1)
    c: DistanceX(g0,g0) = 11.43
    c: DistanceY(g-1,g1) = 5.715
    c: Coincident(g2,g0)
    c: Coincident(g3,g0)
    c: Equal(g3,g2)
    c: Diameter(g2) = 4.2
FEATURE [PartDesign::Pocket] Pocket038  label="Pocket_CSunk_Left_LightMt"
  BaseFeature = -> Pocket037
  Length = 5
  Length2 = 100
  Profile = -> Sketch069
  Type = 1
FEATURE [PartDesign::Pocket] Pocket039  label="Pocket_Csunk_Right_LightMt"
  BaseFeature = -> Pocket038
  Length = 5
  Length2 = 100
  Profile = -> Sketch070
  Type = 1
FEATURE [PartDesign::Body] Body  label="USMt_To_LightSens"
  Group = -> [Sketch,DatumPlane,Sketch064,AdditiveLoft,DatumPlane001,DatumPlane002,Sketch065,Pocket,Sketch066,Pocket034,Sketch067,Pocket035,DatumPlane003,Sketch068,Pocket036,Sketch037,Pocket037,Local_CS,Local_CS001,DatumPlane004,DatumPlane005,Sketch069,Sketch070,Pocket038,Pocket039]
  Origin = -> Origin001
  Placement = pos=(0,0,16.5) rot=(0,0,1;0rad)
  Tip = -> Pocket039
FEATURE [Mesh::Feature] Mesh  label="USMt_To_LightSens (Meshed)"
FEATURE [PartDesign::Plane] DatumPlane006  label="Datum_LightSens_Right001"
  AttachmentOffset = pos=(-35,4.5,0) rot=(0.950144,-0.167536,-0.262979;1.1813rad)
  Length = 98.7976
  MapMode = 5
  Placement = pos=(-35,4.5,0) rot=(0.950144,-0.167536,-0.262979;1.1813rad)
  ResizeMode = 0
  Support = -> [XY_Plane045]
  Width = 90.7209
  expr: .AttachmentOffset.Base.x = <<params>>.lightsens_loc_x * -1
  expr: .AttachmentOffset.Rotation.Yaw = <<params>>.lightsens_ang_z * -1
  expr: .AttachmentOffset.Base.y = <<params>>.lightsens_loc_y
  expr: .AttachmentOffset.Rotation.Roll = <<params>>.lightsens_ang_x
FEATURE [PartDesign::Plane] DatumPlane007  label="Datum_LightSens_Left001"
  AttachmentOffset = pos=(35,4.5,0) rot=(0.950144,0.167536,0.262979;1.1813rad)
  Length = 96.1838
  MapMode = 5
  Placement = pos=(35,4.5,0) rot=(0.950144,0.167536,0.262979;1.1813rad)
  ResizeMode = 0
  Support = -> [XY_Plane045]
  Width = 90.4926
  expr: .AttachmentOffset.Base.x = <<params>>.lightsens_loc_x
  expr: .AttachmentOffset.Rotation.Yaw = <<params>>.lightsens_ang_z
  expr: .AttachmentOffset.Base.y = <<params>>.lightsens_loc_y
  expr: .AttachmentOffset.Base.z = 0mm
  expr: .AttachmentOffset.Rotation.Roll = <<params>>.lightsens_ang_x
FEATURE [Sketcher::SketchObject] Sketch071
  FullyConstrained = true
  MapMode = 5
  Placement = pos=(35,4.5,-4e-16) rot=(0.950144,0.167536,0.262979;1.1813rad)
  Support = -> [DatumPlane007]
  expr: Constraints[15] = <<params>>.lightsens_hole_diam
  expr: Constraints[16] = <<params>>.lightsens_leng
  expr: Constraints[18] = <<params>>.lightsens_leng / 2
  sketch-geometry (9):
    g0: LineSegment StartX=-5.715 StartY=9.255 StartZ=0 EndX=5.715 EndY=9.255 EndZ=0
    g1: LineSegment StartX=8.255 StartY=6.715 StartZ=0 EndX=8.255 EndY=3.54 EndZ=0
    g2: LineSegment StartX=5.715 StartY=1 StartZ=0 EndX=-5.715 EndY=1 EndZ=0
    g3: LineSegment StartX=-8.255 StartY=3.54 StartZ=0 EndX=-8.255 EndY=6.715 EndZ=0
    g4: ArcOfCircle CenterX=-5.715 CenterY=6.715 CenterZ=0 NormalX=0 NormalY=0 NormalZ=1 AngleXU=0 Radius=2.54 StartAngle=1.5708 EndAngle=3.14159
    g5: ArcOfCircle CenterX=5.715 CenterY=6.715 CenterZ=0 NormalX=0 NormalY=0 NormalZ=1 AngleXU=0 Radius=2.54 StartAngle=0 EndAngle=1.5708
    g6: ArcOfCircle CenterX=5.715 CenterY=3.54 CenterZ=0 NormalX=0 NormalY=0 NormalZ=1 AngleXU=0 Radius=2.54 StartAngle=4.71239 EndAngle=6.28319
    g7: ArcOfCircle CenterX=-5.715 CenterY=3.54 CenterZ=0 NormalX=0 NormalY=0 NormalZ=1 AngleXU=0 Radius=2.54 StartAngle=3.14159 EndAngle=4.71239
    g8: GeomPoint X=0 Y=1 Z=0
  constraints (21):
    c: Horizontal(g0)
    c: Horizontal(g2)
    c: Vertical(g1)
    c: Vertical(g3)
    c: Tangent(g3,g4) = 1.5708
    c: Tangent(g0,g4) = 1.5708
    c: Tangent(g0,g5) = 1.5708
    c: Tangent(g1,g5) = 1.5708
    c: Tangent(g1,g6) = 1.5708
    c: Tangent(g2,g6) = 1.5708
    c: Tangent(g2,g7) = 1.5708
    c: Tangent(g3,g7) = 1.5708
    c: Equal(g4,g5)
    c: Equal(g5,g6)
    c: Equal(g6,g7)
    c: Radius(g5) = 2.54
    c: DistanceX(g3,g1) = 16.51
    c: DistanceY(g-1,g2) = 1
    c: DistanceY(g2,g0) = 8.255
    c: PointOnObject(g8,g-2)
    c: Symmetric(g2,g2,g8)
FEATURE [PartDesign::Pad] Pad  label="Pad_Plate"
  Direction = (1,1,1)
  Length = 1.4
  Length2 = 100
  Placement = pos=(35,4.5,0) rot=(0.950144,0.167536,0.262979;1.1813rad)
  Profile = -> Sketch071
  Reversed = true
  Type = 0
FEATURE [Sketcher::SketchObject] Sketch072  label="Sketch_LightMtHoles_L003"
  FullyConstrained = true
  MapMode = 5
  Placement = pos=(35,4.5,-4e-16) rot=(0.950144,0.167536,0.262979;1.1813rad)
  Support = -> [DatumPlane001]
  expr: Constraints[8] = <<params>>.m2_hole_clear_diam
  expr: Constraints[4] = <<params>>.lightsens_width / 2 - <<params>>.lightsens_hole_edge_offset
  expr: Constraints[3] = <<params>>.lightsens_hole_leng_space
  sketch-geometry (4):
    g0: LineSegment StartX=-5.715 StartY=5.715 StartZ=0 EndX=5.715 EndY=5.715 EndZ=0
    g1: GeomPoint X=0 Y=5.715 Z=0
    g2: Circle CenterX=5.715 CenterY=5.715 CenterZ=0 NormalX=0 NormalY=0 NormalZ=1 AngleXU=0 Radius=1.25
    g3: Circle CenterX=-5.715 CenterY=5.715 CenterZ=0 NormalX=0 NormalY=0 NormalZ=1 AngleXU=0 Radius=1.25
  constraints (9):
    c: Horizontal(g0)
    c: PointOnObject(g1,g-2)
    c: Symmetric(g0,g0,g1)
    c: DistanceX(g0,g0) = 11.43
    c: DistanceY(g-1,g1) = 5.715
    c: Coincident(g2,g0)
    c: Coincident(g3,g0)
    c: Equal(g3,g2)
    c: Diameter(g2) = 2.5
FEATURE [PartDesign::Pocket] Pocket040  label="Pocket_Holes"
  BaseFeature = -> Pad
  Length = 5
  Length2 = 100
  Midplane = true
  Placement = pos=(35,4.5,0) rot=(0.950144,0.167536,0.262979;1.1813rad)
  Profile = -> Sketch072
  Type = 1
FEATURE [PartDesign::Body] Body038  label="USMToLS_OffsetPlate_1.4mm"
  Group = -> [DatumPlane006,DatumPlane007,Sketch071,Pad,Sketch072,Pocket040]
  Origin = -> Origin045
  Placement = pos=(0,0,16.5) rot=(0,0,1;0rad)
  Tip = -> Pocket040
FEATURE [PartDesign::Plane] DatumPlane008  label="Datum_LightSens_Left002"
  AttachmentOffset = pos=(35,4.5,0) rot=(0.950144,0.167536,0.262979;1.1813rad)
  Length = 290.523
  MapMode = 5
  Placement = pos=(35,4.5,0) rot=(0.950144,0.167536,0.262979;1.1813rad)
  ResizeMode = 0
  Support = -> [XY_Plane046]
  Width = 321.604
  expr: .AttachmentOffset.Base.x = <<params>>.lightsens_loc_x
  expr: .AttachmentOffset.Rotation.Yaw = <<params>>.lightsens_ang_z
  expr: .AttachmentOffset.Base.y = <<params>>.lightsens_loc_y
  expr: .AttachmentOffset.Base.z = 0mm
  expr: .AttachmentOffset.Rotation.Roll = <<params>>.lightsens_ang_x
FEATURE [Sketcher::SketchObject] Sketch074  label="Sketch_LightMtHoles_L004"
  FullyConstrained = true
  MapMode = 5
  Placement = pos=(35,4.5,-4e-16) rot=(0.950144,0.167536,0.262979;1.1813rad)
  Support = -> [DatumPlane008]
  expr: Constraints[3] = <<params>>.lightsens_hole_leng_space
  expr: Constraints[4] = <<params>>.lightsens_width / 2 - <<params>>.lightsens_hole_edge_offset
  expr: Constraints[8] = <<params>>.m2_hole_clear_diam
  sketch-geometry (4):
    g0: LineSegment StartX=-5.715 StartY=5.715 StartZ=0 EndX=5.715 EndY=5.715 EndZ=0
    g1: GeomPoint X=0 Y=5.715 Z=0
    g2: Circle CenterX=5.715 CenterY=5.715 CenterZ=0 NormalX=0 NormalY=0 NormalZ=1 AngleXU=0 Radius=1.25
    g3: Circle CenterX=-5.715 CenterY=5.715 CenterZ=0 NormalX=0 NormalY=0 NormalZ=1 AngleXU=0 Radius=1.25
  constraints (9):
    c: Horizontal(g0)
    c: PointOnObject(g1,g-2)
    c: Symmetric(g0,g0,g1)
    c: DistanceX(g0,g0) = 11.43
    c: DistanceY(g-1,g1) = 5.715
    c: Coincident(g2,g0)
    c: Coincident(g3,g0)
    c: Equal(g3,g2)
    c: Diameter(g2) = 2.5
FEATURE [PartDesign::Plane] DatumPlane009  label="Datum_LightSens_Right002"
  AttachmentOffset = pos=(-35,4.5,0) rot=(0.950144,-0.167536,-0.262979;1.1813rad)
  Length = 98.7976
  MapMode = 5
  Placement = pos=(-35,4.5,0) rot=(0.950144,-0.167536,-0.262979;1.1813rad)
  ResizeMode = 0
  Support = -> [XY_Plane047]
  Width = 90.7209
  expr: .AttachmentOffset.Rotation.Roll = <<params>>.lightsens_ang_x
  expr: .AttachmentOffset.Base.y = <<params>>.lightsens_loc_y
  expr: .AttachmentOffset.Rotation.Yaw = <<params>>.lightsens_ang_z * -1
  expr: .AttachmentOffset.Base.x = <<params>>.lightsens_loc_x * -1
FEATURE [PartDesign::Plane] DatumPlane010  label="Datum_LightSens_Left003"
  AttachmentOffset = pos=(35,4.5,0) rot=(0.950144,0.167536,0.262979;1.1813rad)
  Length = 96.1838
  MapMode = 5
  Placement = pos=(35,4.5,0) rot=(0.950144,0.167536,0.262979;1.1813rad)
  ResizeMode = 0
  Support = -> [XY_Plane047]
  Width = 90.4926
  expr: .AttachmentOffset.Rotation.Roll = <<params>>.lightsens_ang_x
  expr: .AttachmentOffset.Base.z = 0mm
  expr: .AttachmentOffset.Base.y = <<params>>.lightsens_loc_y
  expr: .AttachmentOffset.Rotation.Yaw = <<params>>.lightsens_ang_z
  expr: .AttachmentOffset.Base.x = <<params>>.lightsens_loc_x
FEATURE [Sketcher::SketchObject] Sketch073
  FullyConstrained = true
  MapMode = 5
  Placement = pos=(35,4.5,4e-16) rot=(0.950144,0.167536,0.262979;1.1813rad)
  Support = -> [DatumPlane010]
  expr: Constraints[18] = <<params>>.lightsens_leng / 2
  expr: Constraints[16] = <<params>>.lightsens_leng
  expr: Constraints[15] = <<params>>.lightsens_hole_diam
  sketch-geometry (9):
    g0: LineSegment StartX=-5.715 StartY=9.255 StartZ=0 EndX=5.715 EndY=9.255 EndZ=0
    g1: LineSegment StartX=8.255 StartY=6.715 StartZ=0 EndX=8.255 EndY=3.54 EndZ=0
    g2: LineSegment StartX=5.715 StartY=1 StartZ=0 EndX=-5.715 EndY=1 EndZ=0
    g3: LineSegment StartX=-8.255 StartY=3.54 StartZ=0 EndX=-8.255 EndY=6.715 EndZ=0
    g4: ArcOfCircle CenterX=-5.715 CenterY=6.715 CenterZ=0 NormalX=0 NormalY=0 NormalZ=1 AngleXU=0 Radius=2.54 StartAngle=1.5708 EndAngle=3.14159
    g5: ArcOfCircle CenterX=5.715 CenterY=6.715 CenterZ=0 NormalX=0 NormalY=0 NormalZ=1 AngleXU=0 Radius=2.54 StartAngle=0 EndAngle=1.5708
    g6: ArcOfCircle CenterX=5.715 CenterY=3.54 CenterZ=0 NormalX=0 NormalY=0 NormalZ=1 AngleXU=0 Radius=2.54 StartAngle=4.71239 EndAngle=6.28319
    g7: ArcOfCircle CenterX=-5.715 CenterY=3.54 CenterZ=0 NormalX=0 NormalY=0 NormalZ=1 AngleXU=0 Radius=2.54 StartAngle=3.14159 EndAngle=4.71239
    g8: GeomPoint X=0 Y=1 Z=0
  constraints (21):
    c: Horizontal(g0)
    c: Horizontal(g2)
    c: Vertical(g1)
    c: Vertical(g3)
    c: Tangent(g3,g4) = 1.5708
    c: Tangent(g0,g4) = 1.5708
    c: Tangent(g0,g5) = 1.5708
    c: Tangent(g1,g5) = 1.5708
    c: Tangent(g1,g6) = 1.5708
    c: Tangent(g2,g6) = 1.5708
    c: Tangent(g2,g7) = 1.5708
    c: Tangent(g3,g7) = 1.5708
    c: Equal(g4,g5)
    c: Equal(g5,g6)
    c: Equal(g6,g7)
    c: Radius(g5) = 2.54
    c: DistanceX(g3,g1) = 16.51
    c: DistanceY(g-1,g2) = 1
    c: DistanceY(g2,g0) = 8.255
    c: PointOnObject(g8,g-2)
    c: Symmetric(g2,g2,g8)
FEATURE [PartDesign::Pad] Pad028  label="Pad_Plate001"
  Direction = (1,1,1)
  Length = 3
  Length2 = 100
  Placement = pos=(35,4.5,0) rot=(0.950144,0.167536,0.262979;1.1813rad)
  Profile = -> Sketch073
  Reversed = true
  Type = 0
FEATURE [PartDesign::Pocket] Pocket041  label="Pocket_Holes001"
  BaseFeature = -> Pad028
  Length = 5
  Length2 = 100
  Midplane = true
  Placement = pos=(35,4.5,0) rot=(0.950144,0.167536,0.262979;1.1813rad)
  Profile = -> Sketch074
  Type = 1
FEATURE [PartDesign::Body] Body039  label="USMToLS_OffsetPlate_3.00mm"
  Group = -> [DatumPlane009,DatumPlane010,Sketch073,Pad028,Sketch074,Pocket041]
  Origin = -> Origin046
  Placement = pos=(0,0,16.5) rot=(0,0,1;0rad)
  Tip = -> Pocket041
FEATURE [App::Part] Part  label="PB3D_USMtToLightSens_Part"
  Group = -> [Body,Body038,Body039]
  Origin = -> Origin
FEATURE [Mesh::Feature] Mesh001  label="USMToLS_OffsetPlate_1.4mm (Meshed)"
